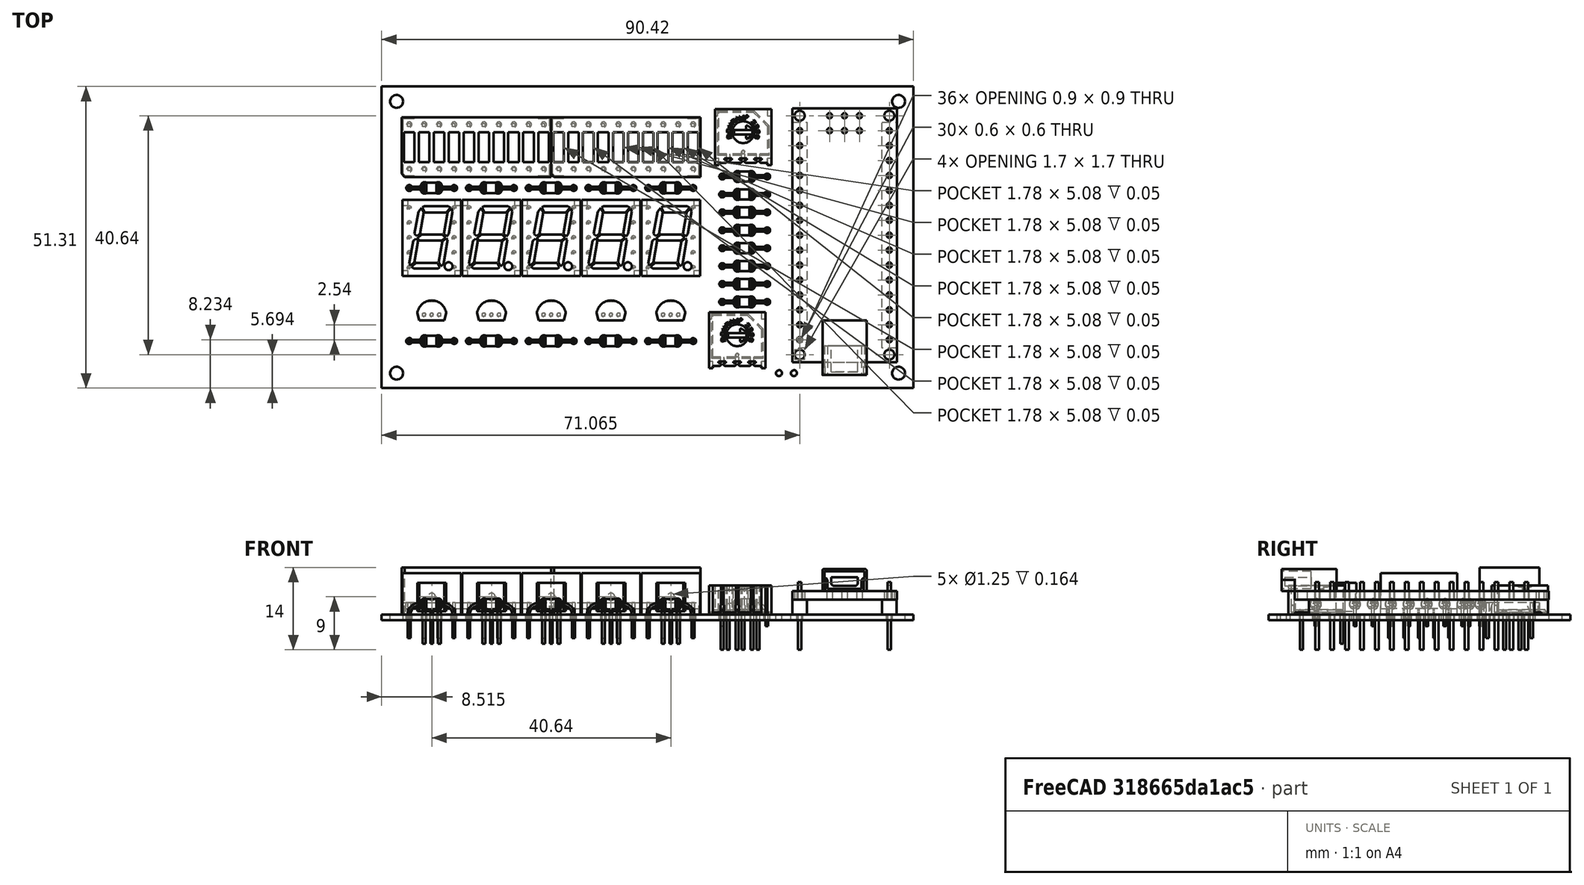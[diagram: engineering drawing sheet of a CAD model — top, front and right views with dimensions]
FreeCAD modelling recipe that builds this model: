
FCSTD DOCUMENT  (FreeCAD 0.16R6707 (Git))
Label: BobaChest
License: All rights reserved
LicenseURL: http://en.wikipedia.org/wiki/All_rights_reserved
objects: Part::Feature×202, Part::Extrusion×187, Part::FeaturePython×29, Drawing::FeatureViewPython×10, App::FeaturePython×8, Part::Compound×4, Part::Part2DObjectPython×2, Drawing::FeatureViewPart×2, Part::MultiFuse×1, Part::Cut×1, App::DocumentObjectGroup×1, Drawing::FeaturePage×1
note: 426 computed .brp shape members not serialized (recipe doc carries the construction recipe); baked Part::Feature solids carry a one-line shape summary decoded from their .brp

FEATURE [Part::Feature] Circle052
  Placement = pos=(33400,-20200,0) rot=(0,0,1;0rad)
  shape: bbox 2.429 x 2.656 x 2e-07 mm, 0 faces, 0 solids (baked)
FEATURE [Part::Feature] Circle053
  Placement = pos=(33400,-38400,0) rot=(0,0,1;0rad)
  shape: bbox 2.429 x 2.656 x 2e-07 mm, 0 faces, 0 solids (baked)
FEATURE [Part::Feature] Circle054
  Placement = pos=(67000,-20200,0) rot=(0,0,1;0rad)
  shape: bbox 2.429 x 2.656 x 2e-07 mm, 0 faces, 0 solids (baked)
FEATURE [Part::Feature] Circle055
  Placement = pos=(67000,-38400,0) rot=(0,0,1;0rad)
  shape: bbox 2.429 x 2.656 x 2e-07 mm, 0 faces, 0 solids (baked)
FEATURE [Part::Feature] Circle132
  Placement = pos=(35750,-34500,0) rot=(0,0,1;0rad)
  shape: bbox 0.701 x 0.7666 x 2e-07 mm, 0 faces, 0 solids (baked)
FEATURE [Part::Feature] Circle133
  Placement = pos=(36250,-34500,0) rot=(0,0,1;0rad)
  shape: bbox 0.701 x 0.7666 x 2e-07 mm, 0 faces, 0 solids (baked)
FEATURE [Part::Feature] Circle134
  Placement = pos=(35250,-34500,0) rot=(0,0,1;0rad)
  shape: bbox 0.701 x 0.7666 x 2e-07 mm, 0 faces, 0 solids (baked)
FEATURE [Part::Feature] Circle135
  Placement = pos=(51750,-34500,0) rot=(0,0,1;0rad)
  shape: bbox 0.701 x 0.7666 x 2e-07 mm, 0 faces, 0 solids (baked)
FEATURE [Part::Feature] Circle136
  Placement = pos=(52250,-34500,0) rot=(0,0,1;0rad)
  shape: bbox 0.701 x 0.7666 x 2e-07 mm, 0 faces, 0 solids (baked)
FEATURE [Part::Feature] Circle137
  Placement = pos=(51250,-34500,0) rot=(0,0,1;0rad)
  shape: bbox 0.701 x 0.7666 x 2e-07 mm, 0 faces, 0 solids (baked)
FEATURE [Part::Feature] Circle138
  Placement = pos=(57200,-36200,0) rot=(0,0,1;0rad)
  shape: bbox 0.701 x 0.7666 x 2e-07 mm, 0 faces, 0 solids (baked)
FEATURE [Part::Feature] Circle139
  Placement = pos=(55200,-36200,0) rot=(0,0,1;0rad)
  shape: bbox 0.701 x 0.7666 x 2e-07 mm, 0 faces, 0 solids (baked)
FEATURE [Part::Feature] Circle140
  Placement = pos=(56200,-37200,0) rot=(0,0,1;0rad)
  shape: bbox 0.701 x 0.7666 x 2e-07 mm, 0 faces, 0 solids (baked)
FEATURE [Part::Feature] Circle141
  Placement = pos=(66380,-36160,0) rot=(0,0,1;0rad)
  shape: bbox 1.122 x 1.227 x 2e-07 mm, 0 faces, 0 solids (baked)
FEATURE [Part::Feature] Circle142
  Placement = pos=(66380,-35160,0) rot=(0,0,1;0rad)
  shape: bbox 1.122 x 1.227 x 2e-07 mm, 0 faces, 0 solids (baked)
FEATURE [Part::Feature] Circle143
  Placement = pos=(66380,-34160,0) rot=(0,0,1;0rad)
  shape: bbox 1.122 x 1.227 x 2e-07 mm, 0 faces, 0 solids (baked)
FEATURE [Part::Feature] Circle144
  Placement = pos=(66380,-33160,0) rot=(0,0,1;0rad)
  shape: bbox 1.122 x 1.227 x 2e-07 mm, 0 faces, 0 solids (baked)
FEATURE [Part::Feature] Circle145
  Placement = pos=(66380,-32160,0) rot=(0,0,1;0rad)
  shape: bbox 1.122 x 1.227 x 2e-07 mm, 0 faces, 0 solids (baked)
FEATURE [Part::Feature] Circle146
  Placement = pos=(66380,-31160,0) rot=(0,0,1;0rad)
  shape: bbox 1.122 x 1.227 x 2e-07 mm, 0 faces, 0 solids (baked)
FEATURE [Part::Feature] Circle147
  Placement = pos=(66380,-30160,0) rot=(0,0,1;0rad)
  shape: bbox 1.122 x 1.227 x 2e-07 mm, 0 faces, 0 solids (baked)
FEATURE [Part::Feature] Circle148
  Placement = pos=(66380,-29160,0) rot=(0,0,1;0rad)
  shape: bbox 1.122 x 1.227 x 2e-07 mm, 0 faces, 0 solids (baked)
FEATURE [Part::Feature] Circle149
  Placement = pos=(66380,-28160,0) rot=(0,0,1;0rad)
  shape: bbox 1.122 x 1.227 x 2e-07 mm, 0 faces, 0 solids (baked)
FEATURE [Part::Feature] Circle150
  Placement = pos=(66380,-27160,0) rot=(0,0,1;0rad)
  shape: bbox 1.122 x 1.227 x 2e-07 mm, 0 faces, 0 solids (baked)
FEATURE [Part::Feature] Circle151
  Placement = pos=(66380,-26160,0) rot=(0,0,1;0rad)
  shape: bbox 1.122 x 1.227 x 2e-07 mm, 0 faces, 0 solids (baked)
FEATURE [Part::Feature] Circle152
  Placement = pos=(66380,-25160,0) rot=(0,0,1;0rad)
  shape: bbox 1.122 x 1.227 x 2e-07 mm, 0 faces, 0 solids (baked)
FEATURE [Part::Feature] Circle153
  Placement = pos=(66380,-24160,0) rot=(0,0,1;0rad)
  shape: bbox 1.122 x 1.227 x 2e-07 mm, 0 faces, 0 solids (baked)
FEATURE [Part::Feature] Circle154
  Placement = pos=(66380,-23160,0) rot=(0,0,1;0rad)
  shape: bbox 1.122 x 1.227 x 2e-07 mm, 0 faces, 0 solids (baked)
FEATURE [Part::Feature] Circle155
  Placement = pos=(66380,-22160,0) rot=(0,0,1;0rad)
  shape: bbox 1.122 x 1.227 x 2e-07 mm, 0 faces, 0 solids (baked)
FEATURE [Part::Feature] Circle156
  Placement = pos=(60380,-22160,0) rot=(0,0,1;0rad)
  shape: bbox 1.122 x 1.227 x 2e-07 mm, 0 faces, 0 solids (baked)
FEATURE [Part::Feature] Circle157
  Placement = pos=(60380,-23160,0) rot=(0,0,1;0rad)
  shape: bbox 1.122 x 1.227 x 2e-07 mm, 0 faces, 0 solids (baked)
FEATURE [Part::Feature] Circle158
  Placement = pos=(60380,-24160,0) rot=(0,0,1;0rad)
  shape: bbox 1.122 x 1.227 x 2e-07 mm, 0 faces, 0 solids (baked)
FEATURE [Part::Feature] Circle159
  Placement = pos=(60380,-25160,0) rot=(0,0,1;0rad)
  shape: bbox 1.122 x 1.227 x 2e-07 mm, 0 faces, 0 solids (baked)
FEATURE [Part::Feature] Circle160
  Placement = pos=(60380,-26160,0) rot=(0,0,1;0rad)
  shape: bbox 1.122 x 1.227 x 2e-07 mm, 0 faces, 0 solids (baked)
FEATURE [Part::Feature] Circle161
  Placement = pos=(60380,-27160,0) rot=(0,0,1;0rad)
  shape: bbox 1.122 x 1.227 x 2e-07 mm, 0 faces, 0 solids (baked)
FEATURE [Part::Feature] Circle162
  Placement = pos=(60380,-28160,0) rot=(0,0,1;0rad)
  shape: bbox 1.122 x 1.227 x 2e-07 mm, 0 faces, 0 solids (baked)
FEATURE [Part::Feature] Circle163
  Placement = pos=(60380,-29160,0) rot=(0,0,1;0rad)
  shape: bbox 1.122 x 1.227 x 2e-07 mm, 0 faces, 0 solids (baked)
FEATURE [Part::Feature] Circle164
  Placement = pos=(60380,-30160,0) rot=(0,0,1;0rad)
  shape: bbox 1.122 x 1.227 x 2e-07 mm, 0 faces, 0 solids (baked)
FEATURE [Part::Feature] Circle165
  Placement = pos=(60380,-31160,0) rot=(0,0,1;0rad)
  shape: bbox 1.122 x 1.227 x 2e-07 mm, 0 faces, 0 solids (baked)
FEATURE [Part::Feature] Circle166
  Placement = pos=(60380,-32160,0) rot=(0,0,1;0rad)
  shape: bbox 1.122 x 1.227 x 2e-07 mm, 0 faces, 0 solids (baked)
FEATURE [Part::Feature] Circle167
  Placement = pos=(60380,-33160,0) rot=(0,0,1;0rad)
  shape: bbox 1.122 x 1.227 x 2e-07 mm, 0 faces, 0 solids (baked)
FEATURE [Part::Feature] Circle168
  Placement = pos=(60380,-34160,0) rot=(0,0,1;0rad)
  shape: bbox 1.122 x 1.227 x 2e-07 mm, 0 faces, 0 solids (baked)
FEATURE [Part::Feature] Circle169
  Placement = pos=(60380,-35160,0) rot=(0,0,1;0rad)
  shape: bbox 1.122 x 1.227 x 2e-07 mm, 0 faces, 0 solids (baked)
FEATURE [Part::Feature] Circle170
  Placement = pos=(60380,-36160,0) rot=(0,0,1;0rad)
  shape: bbox 1.122 x 1.227 x 2e-07 mm, 0 faces, 0 solids (baked)
FEATURE [Part::Feature] Circle171
  Placement = pos=(39750,-34500,0) rot=(0,0,1;0rad)
  shape: bbox 0.701 x 0.7666 x 2e-07 mm, 0 faces, 0 solids (baked)
FEATURE [Part::Feature] Circle172
  Placement = pos=(40250,-34500,0) rot=(0,0,1;0rad)
  shape: bbox 0.701 x 0.7666 x 2e-07 mm, 0 faces, 0 solids (baked)
FEATURE [Part::Feature] Circle173
  Placement = pos=(39250,-34500,0) rot=(0,0,1;0rad)
  shape: bbox 0.701 x 0.7666 x 2e-07 mm, 0 faces, 0 solids (baked)
FEATURE [Part::Feature] Circle174
  Placement = pos=(43750,-34500,0) rot=(0,0,1;0rad)
  shape: bbox 0.701 x 0.7666 x 2e-07 mm, 0 faces, 0 solids (baked)
FEATURE [Part::Feature] Circle175
  Placement = pos=(44250,-34500,0) rot=(0,0,1;0rad)
  shape: bbox 0.701 x 0.7666 x 2e-07 mm, 0 faces, 0 solids (baked)
FEATURE [Part::Feature] Circle176
  Placement = pos=(43250,-34500,0) rot=(0,0,1;0rad)
  shape: bbox 0.701 x 0.7666 x 2e-07 mm, 0 faces, 0 solids (baked)
FEATURE [Part::Feature] Circle177
  Placement = pos=(47750,-34500,0) rot=(0,0,1;0rad)
  shape: bbox 0.701 x 0.7666 x 2e-07 mm, 0 faces, 0 solids (baked)
FEATURE [Part::Feature] Circle178
  Placement = pos=(48250,-34500,0) rot=(0,0,1;0rad)
  shape: bbox 0.701 x 0.7666 x 2e-07 mm, 0 faces, 0 solids (baked)
FEATURE [Part::Feature] Circle179
  Placement = pos=(47250,-34500,0) rot=(0,0,1;0rad)
  shape: bbox 0.701 x 0.7666 x 2e-07 mm, 0 faces, 0 solids (baked)
FEATURE [Part::Feature] Circle180
  Placement = pos=(42250,-27345.3,0) rot=(0,0,1;0rad)
  shape: bbox 0.8413 x 0.9199 x 2e-07 mm, 0 faces, 0 solids (baked)
FEATURE [Part::Feature] Circle181
  Placement = pos=(45250,-27345.3,0) rot=(0,0,1;0rad)
  shape: bbox 0.8413 x 0.9199 x 2e-07 mm, 0 faces, 0 solids (baked)
FEATURE [Part::Feature] Circle182
  Placement = pos=(42250,-28345.3,0) rot=(0,0,1;0rad)
  shape: bbox 0.8413 x 0.9199 x 2e-07 mm, 0 faces, 0 solids (baked)
FEATURE [Part::Feature] Circle183
  Placement = pos=(45250,-28345.3,0) rot=(0,0,1;0rad)
  shape: bbox 0.8413 x 0.9199 x 2e-07 mm, 0 faces, 0 solids (baked)
FEATURE [Part::Feature] Circle184
  Placement = pos=(42250,-29345.3,0) rot=(0,0,1;0rad)
  shape: bbox 0.8413 x 0.9199 x 2e-07 mm, 0 faces, 0 solids (baked)
FEATURE [Part::Feature] Circle185
  Placement = pos=(45250,-29345.3,0) rot=(0,0,1;0rad)
  shape: bbox 0.8413 x 0.9199 x 2e-07 mm, 0 faces, 0 solids (baked)
FEATURE [Part::Feature] Circle186
  Placement = pos=(42250,-30345.3,0) rot=(0,0,1;0rad)
  shape: bbox 0.8413 x 0.9199 x 2e-07 mm, 0 faces, 0 solids (baked)
FEATURE [Part::Feature] Circle187
  Placement = pos=(45250,-30345.3,0) rot=(0,0,1;0rad)
  shape: bbox 0.8413 x 0.9199 x 2e-07 mm, 0 faces, 0 solids (baked)
FEATURE [Part::Feature] Circle188
  Placement = pos=(42250,-31345.3,0) rot=(0,0,1;0rad)
  shape: bbox 0.8413 x 0.9199 x 2e-07 mm, 0 faces, 0 solids (baked)
FEATURE [Part::Feature] Circle189
  Placement = pos=(45250,-31345.3,0) rot=(0,0,1;0rad)
  shape: bbox 0.8413 x 0.9199 x 2e-07 mm, 0 faces, 0 solids (baked)
FEATURE [Part::Feature] Circle190
  Placement = pos=(50250,-27345.3,0) rot=(0,0,1;0rad)
  shape: bbox 0.8413 x 0.9199 x 2e-07 mm, 0 faces, 0 solids (baked)
FEATURE [Part::Feature] Circle191
  Placement = pos=(53250,-27345.3,0) rot=(0,0,1;0rad)
  shape: bbox 0.8413 x 0.9199 x 2e-07 mm, 0 faces, 0 solids (baked)
FEATURE [Part::Feature] Circle192
  Placement = pos=(50250,-28345.3,0) rot=(0,0,1;0rad)
  shape: bbox 0.8413 x 0.9199 x 2e-07 mm, 0 faces, 0 solids (baked)
FEATURE [Part::Feature] Circle193
  Placement = pos=(53250,-28345.3,0) rot=(0,0,1;0rad)
  shape: bbox 0.8413 x 0.9199 x 2e-07 mm, 0 faces, 0 solids (baked)
FEATURE [Part::Feature] Circle194
  Placement = pos=(50250,-29345.3,0) rot=(0,0,1;0rad)
  shape: bbox 0.8413 x 0.9199 x 2e-07 mm, 0 faces, 0 solids (baked)
FEATURE [Part::Feature] Circle195
  Placement = pos=(53250,-29345.3,0) rot=(0,0,1;0rad)
  shape: bbox 0.8413 x 0.9199 x 2e-07 mm, 0 faces, 0 solids (baked)
FEATURE [Part::Feature] Circle196
  Placement = pos=(50250,-30345.3,0) rot=(0,0,1;0rad)
  shape: bbox 0.8413 x 0.9199 x 2e-07 mm, 0 faces, 0 solids (baked)
FEATURE [Part::Feature] Circle197
  Placement = pos=(53250,-30345.3,0) rot=(0,0,1;0rad)
  shape: bbox 0.8413 x 0.9199 x 2e-07 mm, 0 faces, 0 solids (baked)
FEATURE [Part::Feature] Circle198
  Placement = pos=(50250,-31345.3,0) rot=(0,0,1;0rad)
  shape: bbox 0.8413 x 0.9199 x 2e-07 mm, 0 faces, 0 solids (baked)
FEATURE [Part::Feature] Circle199
  Placement = pos=(53250,-31345.3,0) rot=(0,0,1;0rad)
  shape: bbox 0.8413 x 0.9199 x 2e-07 mm, 0 faces, 0 solids (baked)
FEATURE [Part::Feature] Circle200
  Placement = pos=(46250,-27345.3,0) rot=(0,0,1;0rad)
  shape: bbox 0.8413 x 0.9199 x 2e-07 mm, 0 faces, 0 solids (baked)
FEATURE [Part::Feature] Circle201
  Placement = pos=(49250,-27345.3,0) rot=(0,0,1;0rad)
  shape: bbox 0.8413 x 0.9199 x 2e-07 mm, 0 faces, 0 solids (baked)
FEATURE [Part::Feature] Circle202
  Placement = pos=(46250,-28345.3,0) rot=(0,0,1;0rad)
  shape: bbox 0.8413 x 0.9199 x 2e-07 mm, 0 faces, 0 solids (baked)
FEATURE [Part::Feature] Circle203
  Placement = pos=(49250,-28345.3,0) rot=(0,0,1;0rad)
  shape: bbox 0.8413 x 0.9199 x 2e-07 mm, 0 faces, 0 solids (baked)
FEATURE [Part::Feature] Circle204
  Placement = pos=(46250,-29345.3,0) rot=(0,0,1;0rad)
  shape: bbox 0.8413 x 0.9199 x 2e-07 mm, 0 faces, 0 solids (baked)
FEATURE [Part::Feature] Circle205
  Placement = pos=(49250,-29345.3,0) rot=(0,0,1;0rad)
  shape: bbox 0.8413 x 0.9199 x 2e-07 mm, 0 faces, 0 solids (baked)
FEATURE [Part::Feature] Circle206
  Placement = pos=(46250,-30345.3,0) rot=(0,0,1;0rad)
  shape: bbox 0.8413 x 0.9199 x 2e-07 mm, 0 faces, 0 solids (baked)
FEATURE [Part::Feature] Circle207
  Placement = pos=(49250,-30345.3,0) rot=(0,0,1;0rad)
  shape: bbox 0.8413 x 0.9199 x 2e-07 mm, 0 faces, 0 solids (baked)
FEATURE [Part::Feature] Circle208
  Placement = pos=(46250,-31345.3,0) rot=(0,0,1;0rad)
  shape: bbox 0.8413 x 0.9199 x 2e-07 mm, 0 faces, 0 solids (baked)
FEATURE [Part::Feature] Circle209
  Placement = pos=(49250,-31345.3,0) rot=(0,0,1;0rad)
  shape: bbox 0.8413 x 0.9199 x 2e-07 mm, 0 faces, 0 solids (baked)
FEATURE [Part::Feature] Circle210
  Placement = pos=(38250,-27345.3,0) rot=(0,0,1;0rad)
  shape: bbox 0.8413 x 0.9199 x 2e-07 mm, 0 faces, 0 solids (baked)
FEATURE [Part::Feature] Circle211
  Placement = pos=(41250,-27345.3,0) rot=(0,0,1;0rad)
  shape: bbox 0.8413 x 0.9199 x 2e-07 mm, 0 faces, 0 solids (baked)
FEATURE [Part::Feature] Circle212
  Placement = pos=(38250,-28345.3,0) rot=(0,0,1;0rad)
  shape: bbox 0.8413 x 0.9199 x 2e-07 mm, 0 faces, 0 solids (baked)
FEATURE [Part::Feature] Circle213
  Placement = pos=(41250,-28345.3,0) rot=(0,0,1;0rad)
  shape: bbox 0.8413 x 0.9199 x 2e-07 mm, 0 faces, 0 solids (baked)
FEATURE [Part::Feature] Circle214
  Placement = pos=(38250,-29345.3,0) rot=(0,0,1;0rad)
  shape: bbox 0.8413 x 0.9199 x 2e-07 mm, 0 faces, 0 solids (baked)
FEATURE [Part::Feature] Circle215
  Placement = pos=(41250,-29345.3,0) rot=(0,0,1;0rad)
  shape: bbox 0.8413 x 0.9199 x 2e-07 mm, 0 faces, 0 solids (baked)
FEATURE [Part::Feature] Circle216
  Placement = pos=(38250,-30345.3,0) rot=(0,0,1;0rad)
  shape: bbox 0.8413 x 0.9199 x 2e-07 mm, 0 faces, 0 solids (baked)
FEATURE [Part::Feature] Circle217
  Placement = pos=(41250,-30345.3,0) rot=(0,0,1;0rad)
  shape: bbox 0.8413 x 0.9199 x 2e-07 mm, 0 faces, 0 solids (baked)
FEATURE [Part::Feature] Circle218
  Placement = pos=(38250,-31345.3,0) rot=(0,0,1;0rad)
  shape: bbox 0.8413 x 0.9199 x 2e-07 mm, 0 faces, 0 solids (baked)
FEATURE [Part::Feature] Circle219
  Placement = pos=(41250,-31345.3,0) rot=(0,0,1;0rad)
  shape: bbox 0.8413 x 0.9199 x 2e-07 mm, 0 faces, 0 solids (baked)
FEATURE [Part::Feature] Circle220
  Placement = pos=(34250,-27345.3,0) rot=(0,0,1;0rad)
  shape: bbox 0.8413 x 0.9199 x 2e-07 mm, 0 faces, 0 solids (baked)
FEATURE [Part::Feature] Circle221
  Placement = pos=(37250,-27345.3,0) rot=(0,0,1;0rad)
  shape: bbox 0.8413 x 0.9199 x 2e-07 mm, 0 faces, 0 solids (baked)
FEATURE [Part::Feature] Circle222
  Placement = pos=(34250,-28345.3,0) rot=(0,0,1;0rad)
  shape: bbox 0.8413 x 0.9199 x 2e-07 mm, 0 faces, 0 solids (baked)
FEATURE [Part::Feature] Circle223
  Placement = pos=(37250,-28345.3,0) rot=(0,0,1;0rad)
  shape: bbox 0.8413 x 0.9199 x 2e-07 mm, 0 faces, 0 solids (baked)
FEATURE [Part::Feature] Circle224
  Placement = pos=(34250,-29345.3,0) rot=(0,0,1;0rad)
  shape: bbox 0.8413 x 0.9199 x 2e-07 mm, 0 faces, 0 solids (baked)
FEATURE [Part::Feature] Circle225
  Placement = pos=(37250,-29345.3,0) rot=(0,0,1;0rad)
  shape: bbox 0.8413 x 0.9199 x 2e-07 mm, 0 faces, 0 solids (baked)
FEATURE [Part::Feature] Circle226
  Placement = pos=(34250,-30345.3,0) rot=(0,0,1;0rad)
  shape: bbox 0.8413 x 0.9199 x 2e-07 mm, 0 faces, 0 solids (baked)
FEATURE [Part::Feature] Circle227
  Placement = pos=(37250,-30345.3,0) rot=(0,0,1;0rad)
  shape: bbox 0.8413 x 0.9199 x 2e-07 mm, 0 faces, 0 solids (baked)
FEATURE [Part::Feature] Circle228
  Placement = pos=(34250,-31345.3,0) rot=(0,0,1;0rad)
  shape: bbox 0.8413 x 0.9199 x 2e-07 mm, 0 faces, 0 solids (baked)
FEATURE [Part::Feature] Circle229
  Placement = pos=(37250,-31345.3,0) rot=(0,0,1;0rad)
  shape: bbox 0.8413 x 0.9199 x 2e-07 mm, 0 faces, 0 solids (baked)
FEATURE [Part::Feature] Circle230
  Placement = pos=(60000,-38400,0) rot=(0,0,1;0rad)
  shape: bbox 1.122 x 1.227 x 2e-07 mm, 0 faces, 0 solids (baked)
FEATURE [Part::Feature] Circle231
  Placement = pos=(59000,-38400,0) rot=(0,0,1;0rad)
  shape: bbox 1.122 x 1.227 x 2e-07 mm, 0 faces, 0 solids (baked)
FEATURE [Part::Feature] Circle232
  Placement = pos=(33400,-20200,0) rot=(0,0,1;0rad)
  shape: bbox 2.429 x 2.656 x 2e-07 mm, 0 faces, 0 solids (baked)
FEATURE [Part::Feature] Circle233
  Placement = pos=(33400,-38400,0) rot=(0,0,1;0rad)
  shape: bbox 2.429 x 2.656 x 2e-07 mm, 0 faces, 0 solids (baked)
FEATURE [Part::Feature] Circle234
  Placement = pos=(67000,-20200,0) rot=(0,0,1;0rad)
  shape: bbox 2.429 x 2.656 x 2e-07 mm, 0 faces, 0 solids (baked)
FEATURE [Part::Feature] Circle235
  Placement = pos=(67000,-38400,0) rot=(0,0,1;0rad)
  shape: bbox 2.429 x 2.656 x 2e-07 mm, 0 faces, 0 solids (baked)
FEATURE [Part::Feature] Circle237
  Placement = pos=(35250,-24750,0) rot=(0,0,1;0rad)
  shape: bbox 1.01 x 1.104 x 2e-07 mm, 0 faces, 0 solids (baked)
FEATURE [Part::Feature] Circle238
  Placement = pos=(36250,-24750,0) rot=(0,0,1;0rad)
  shape: bbox 1.01 x 1.104 x 2e-07 mm, 0 faces, 0 solids (baked)
FEATURE [Part::Feature] Circle239
  Placement = pos=(37250,-24750,0) rot=(0,0,1;0rad)
  shape: bbox 1.01 x 1.104 x 2e-07 mm, 0 faces, 0 solids (baked)
FEATURE [Part::Feature] Circle240
  Placement = pos=(41250,-21750,0) rot=(0,0,1;0rad)
  shape: bbox 1.01 x 1.104 x 2e-07 mm, 0 faces, 0 solids (baked)
FEATURE [Part::Feature] Circle241
  Placement = pos=(40250,-21750,0) rot=(0,0,1;0rad)
  shape: bbox 1.01 x 1.104 x 2e-07 mm, 0 faces, 0 solids (baked)
FEATURE [Part::Feature] Circle242
  Placement = pos=(39250,-21750,0) rot=(0,0,1;0rad)
  shape: bbox 1.01 x 1.104 x 2e-07 mm, 0 faces, 0 solids (baked)
FEATURE [Part::Feature] Circle243
  Placement = pos=(38250,-21750,0) rot=(0,0,1;0rad)
  shape: bbox 1.01 x 1.104 x 2e-07 mm, 0 faces, 0 solids (baked)
FEATURE [Part::Feature] Circle244
  Placement = pos=(38250,-24750,0) rot=(0,0,1;0rad)
  shape: bbox 1.01 x 1.104 x 2e-07 mm, 0 faces, 0 solids (baked)
FEATURE [Part::Feature] Circle245
  Placement = pos=(39250,-24750,0) rot=(0,0,1;0rad)
  shape: bbox 1.01 x 1.104 x 2e-07 mm, 0 faces, 0 solids (baked)
FEATURE [Part::Feature] Circle246
  Placement = pos=(40250,-24750,0) rot=(0,0,1;0rad)
  shape: bbox 1.01 x 1.104 x 2e-07 mm, 0 faces, 0 solids (baked)
FEATURE [Part::Feature] Circle247
  Placement = pos=(41250,-24750,0) rot=(0,0,1;0rad)
  shape: bbox 1.01 x 1.104 x 2e-07 mm, 0 faces, 0 solids (baked)
FEATURE [Part::Feature] Circle248
  Placement = pos=(42250,-21750,0) rot=(0,0,1;0rad)
  shape: bbox 1.01 x 1.104 x 2e-07 mm, 0 faces, 0 solids (baked)
FEATURE [Part::Feature] Circle249
  Placement = pos=(43250,-21750,0) rot=(0,0,1;0rad)
  shape: bbox 1.01 x 1.104 x 2e-07 mm, 0 faces, 0 solids (baked)
FEATURE [Part::Feature] Circle250
  Placement = pos=(43250,-24750,0) rot=(0,0,1;0rad)
  shape: bbox 1.01 x 1.104 x 2e-07 mm, 0 faces, 0 solids (baked)
FEATURE [Part::Feature] Circle251
  Placement = pos=(42250,-24750,0) rot=(0,0,1;0rad)
  shape: bbox 1.01 x 1.104 x 2e-07 mm, 0 faces, 0 solids (baked)
FEATURE [Part::Feature] Circle252
  Placement = pos=(37250,-21750,0) rot=(0,0,1;0rad)
  shape: bbox 1.01 x 1.104 x 2e-07 mm, 0 faces, 0 solids (baked)
FEATURE [Part::Feature] Circle253
  Placement = pos=(36250,-21750,0) rot=(0,0,1;0rad)
  shape: bbox 1.01 x 1.104 x 2e-07 mm, 0 faces, 0 solids (baked)
FEATURE [Part::Feature] Circle254
  Placement = pos=(35250,-21750,0) rot=(0,0,1;0rad)
  shape: bbox 1.01 x 1.104 x 2e-07 mm, 0 faces, 0 solids (baked)
FEATURE [Part::Feature] Circle255
  Placement = pos=(34250,-21750,0) rot=(0,0,1;0rad)
  shape: bbox 1.01 x 1.104 x 2e-07 mm, 0 faces, 0 solids (baked)
FEATURE [Part::Feature] Circle256
  Placement = pos=(44250,-24750,0) rot=(0,0,1;0rad)
  shape: bbox 1.01 x 1.104 x 2e-07 mm, 0 faces, 0 solids (baked)
FEATURE [Part::Feature] Circle257
  Placement = pos=(45250,-24750,0) rot=(0,0,1;0rad)
  shape: bbox 1.01 x 1.104 x 2e-07 mm, 0 faces, 0 solids (baked)
FEATURE [Part::Feature] Circle258
  Placement = pos=(46250,-24750,0) rot=(0,0,1;0rad)
  shape: bbox 1.01 x 1.104 x 2e-07 mm, 0 faces, 0 solids (baked)
FEATURE [Part::Feature] Circle259
  Placement = pos=(47250,-24750,0) rot=(0,0,1;0rad)
  shape: bbox 1.01 x 1.104 x 2e-07 mm, 0 faces, 0 solids (baked)
FEATURE [Part::Feature] Circle260
  Placement = pos=(51250,-21750,0) rot=(0,0,1;0rad)
  shape: bbox 1.01 x 1.104 x 2e-07 mm, 0 faces, 0 solids (baked)
FEATURE [Part::Feature] Circle261
  Placement = pos=(50250,-21750,0) rot=(0,0,1;0rad)
  shape: bbox 1.01 x 1.104 x 2e-07 mm, 0 faces, 0 solids (baked)
FEATURE [Part::Feature] Circle262
  Placement = pos=(49250,-21750,0) rot=(0,0,1;0rad)
  shape: bbox 1.01 x 1.104 x 2e-07 mm, 0 faces, 0 solids (baked)
FEATURE [Part::Feature] Circle263
  Placement = pos=(48250,-21750,0) rot=(0,0,1;0rad)
  shape: bbox 1.01 x 1.104 x 2e-07 mm, 0 faces, 0 solids (baked)
FEATURE [Part::Feature] Circle264
  Placement = pos=(48250,-24750,0) rot=(0,0,1;0rad)
  shape: bbox 1.01 x 1.104 x 2e-07 mm, 0 faces, 0 solids (baked)
FEATURE [Part::Feature] Circle265
  Placement = pos=(49250,-24750,0) rot=(0,0,1;0rad)
  shape: bbox 1.01 x 1.104 x 2e-07 mm, 0 faces, 0 solids (baked)
FEATURE [Part::Feature] Circle266
  Placement = pos=(50250,-24750,0) rot=(0,0,1;0rad)
  shape: bbox 1.01 x 1.104 x 2e-07 mm, 0 faces, 0 solids (baked)
FEATURE [Part::Feature] Circle267
  Placement = pos=(51250,-24750,0) rot=(0,0,1;0rad)
  shape: bbox 1.01 x 1.104 x 2e-07 mm, 0 faces, 0 solids (baked)
FEATURE [Part::Feature] Circle268
  Placement = pos=(52250,-21750,0) rot=(0,0,1;0rad)
  shape: bbox 1.01 x 1.104 x 2e-07 mm, 0 faces, 0 solids (baked)
FEATURE [Part::Feature] Circle269
  Placement = pos=(53250,-21750,0) rot=(0,0,1;0rad)
  shape: bbox 1.01 x 1.104 x 2e-07 mm, 0 faces, 0 solids (baked)
FEATURE [Part::Feature] Circle270
  Placement = pos=(53250,-24750,0) rot=(0,0,1;0rad)
  shape: bbox 1.01 x 1.104 x 2e-07 mm, 0 faces, 0 solids (baked)
FEATURE [Part::Feature] Circle271
  Placement = pos=(52250,-24750,0) rot=(0,0,1;0rad)
  shape: bbox 1.01 x 1.104 x 2e-07 mm, 0 faces, 0 solids (baked)
FEATURE [Part::Feature] Circle272
  Placement = pos=(47250,-21750,0) rot=(0,0,1;0rad)
  shape: bbox 1.01 x 1.104 x 2e-07 mm, 0 faces, 0 solids (baked)
FEATURE [Part::Feature] Circle273
  Placement = pos=(46250,-21750,0) rot=(0,0,1;0rad)
  shape: bbox 1.01 x 1.104 x 2e-07 mm, 0 faces, 0 solids (baked)
FEATURE [Part::Feature] Circle274
  Placement = pos=(45250,-21750,0) rot=(0,0,1;0rad)
  shape: bbox 1.01 x 1.104 x 2e-07 mm, 0 faces, 0 solids (baked)
FEATURE [Part::Feature] Circle275
  Placement = pos=(44250,-21750,0) rot=(0,0,1;0rad)
  shape: bbox 1.01 x 1.104 x 2e-07 mm, 0 faces, 0 solids (baked)
FEATURE [Part::Feature] Circle276
  Placement = pos=(57600,-22600,0) rot=(0,0,1;0rad)
  shape: bbox 0.701 x 0.7666 x 2e-07 mm, 0 faces, 0 solids (baked)
FEATURE [Part::Feature] Circle277
  Placement = pos=(55600,-22600,0) rot=(0,0,1;0rad)
  shape: bbox 0.701 x 0.7666 x 2e-07 mm, 0 faces, 0 solids (baked)
FEATURE [Part::Feature] Circle278
  Placement = pos=(56600,-23600,0) rot=(0,0,1;0rad)
  shape: bbox 0.701 x 0.7666 x 2e-07 mm, 0 faces, 0 solids (baked)
FEATURE [Part::Feature] Circle279
  Placement = pos=(55200,-26430,0) rot=(0,0,1;0rad)
  shape: bbox 1.122 x 1.227 x 2e-07 mm, 0 faces, 0 solids (baked)
FEATURE [Part::Feature] Circle280
  Placement = pos=(58200,-26430,0) rot=(0,0,1;0rad)
  shape: bbox 1.122 x 1.227 x 2e-07 mm, 0 faces, 0 solids (baked)
FEATURE [Part::Feature] Circle281
  Placement = pos=(55200,-28830,0) rot=(0,0,1;0rad)
  shape: bbox 1.122 x 1.227 x 2e-07 mm, 0 faces, 0 solids (baked)
FEATURE [Part::Feature] Circle282
  Placement = pos=(58200,-28830,0) rot=(0,0,1;0rad)
  shape: bbox 1.122 x 1.227 x 2e-07 mm, 0 faces, 0 solids (baked)
FEATURE [Part::Feature] Circle283
  Placement = pos=(55200,-31230,0) rot=(0,0,1;0rad)
  shape: bbox 1.122 x 1.227 x 2e-07 mm, 0 faces, 0 solids (baked)
FEATURE [Part::Feature] Circle284
  Placement = pos=(58200,-31230,0) rot=(0,0,1;0rad)
  shape: bbox 1.122 x 1.227 x 2e-07 mm, 0 faces, 0 solids (baked)
FEATURE [Part::Feature] Circle285
  Placement = pos=(55200,-32430,0) rot=(0,0,1;0rad)
  shape: bbox 1.122 x 1.227 x 2e-07 mm, 0 faces, 0 solids (baked)
FEATURE [Part::Feature] Circle286
  Placement = pos=(58200,-32430,0) rot=(0,0,1;0rad)
  shape: bbox 1.122 x 1.227 x 2e-07 mm, 0 faces, 0 solids (baked)
FEATURE [Part::Feature] Circle287
  Placement = pos=(55200,-30030,0) rot=(0,0,1;0rad)
  shape: bbox 1.122 x 1.227 x 2e-07 mm, 0 faces, 0 solids (baked)
FEATURE [Part::Feature] Circle288
  Placement = pos=(58200,-30030,0) rot=(0,0,1;0rad)
  shape: bbox 1.122 x 1.227 x 2e-07 mm, 0 faces, 0 solids (baked)
FEATURE [Part::Feature] Circle289
  Placement = pos=(55200,-27630,0) rot=(0,0,1;0rad)
  shape: bbox 1.122 x 1.227 x 2e-07 mm, 0 faces, 0 solids (baked)
FEATURE [Part::Feature] Circle290
  Placement = pos=(58200,-27630,0) rot=(0,0,1;0rad)
  shape: bbox 1.122 x 1.227 x 2e-07 mm, 0 faces, 0 solids (baked)
FEATURE [Part::Feature] Circle291
  Placement = pos=(55200,-25230,0) rot=(0,0,1;0rad)
  shape: bbox 1.122 x 1.227 x 2e-07 mm, 0 faces, 0 solids (baked)
FEATURE [Part::Feature] Circle292
  Placement = pos=(58200,-25230,0) rot=(0,0,1;0rad)
  shape: bbox 1.122 x 1.227 x 2e-07 mm, 0 faces, 0 solids (baked)
FEATURE [Part::Feature] Circle293
  Placement = pos=(55200,-33630,0) rot=(0,0,1;0rad)
  shape: bbox 1.122 x 1.227 x 2e-07 mm, 0 faces, 0 solids (baked)
FEATURE [Part::Feature] Circle294
  Placement = pos=(58200,-33630,0) rot=(0,0,1;0rad)
  shape: bbox 1.122 x 1.227 x 2e-07 mm, 0 faces, 0 solids (baked)
FEATURE [Part::Feature] Circle295
  Placement = pos=(50250,-26000,0) rot=(0,0,1;0rad)
  shape: bbox 1.122 x 1.227 x 2e-07 mm, 0 faces, 0 solids (baked)
FEATURE [Part::Feature] Circle296
  Placement = pos=(53250,-26000,0) rot=(0,0,1;0rad)
  shape: bbox 1.122 x 1.227 x 2e-07 mm, 0 faces, 0 solids (baked)
FEATURE [Part::Feature] Circle297
  Placement = pos=(46250,-26000,0) rot=(0,0,1;0rad)
  shape: bbox 1.122 x 1.227 x 2e-07 mm, 0 faces, 0 solids (baked)
FEATURE [Part::Feature] Circle298
  Placement = pos=(49250,-26000,0) rot=(0,0,1;0rad)
  shape: bbox 1.122 x 1.227 x 2e-07 mm, 0 faces, 0 solids (baked)
FEATURE [Part::Feature] Circle299
  Placement = pos=(42250,-26000,0) rot=(0,0,1;0rad)
  shape: bbox 1.122 x 1.227 x 2e-07 mm, 0 faces, 0 solids (baked)
FEATURE [Part::Feature] Circle300
  Placement = pos=(45250,-26000,0) rot=(0,0,1;0rad)
  shape: bbox 1.122 x 1.227 x 2e-07 mm, 0 faces, 0 solids (baked)
FEATURE [Part::Feature] Circle301
  Placement = pos=(38250,-26000,0) rot=(0,0,1;0rad)
  shape: bbox 1.122 x 1.227 x 2e-07 mm, 0 faces, 0 solids (baked)
FEATURE [Part::Feature] Circle302
  Placement = pos=(41250,-26000,0) rot=(0,0,1;0rad)
  shape: bbox 1.122 x 1.227 x 2e-07 mm, 0 faces, 0 solids (baked)
FEATURE [Part::Feature] Circle303
  Placement = pos=(34250,-26000,0) rot=(0,0,1;0rad)
  shape: bbox 1.122 x 1.227 x 2e-07 mm, 0 faces, 0 solids (baked)
FEATURE [Part::Feature] Circle304
  Placement = pos=(37250,-26000,0) rot=(0,0,1;0rad)
  shape: bbox 1.122 x 1.227 x 2e-07 mm, 0 faces, 0 solids (baked)
FEATURE [Part::Feature] Circle305
  Placement = pos=(50250,-36250,0) rot=(0,0,1;0rad)
  shape: bbox 1.122 x 1.227 x 2e-07 mm, 0 faces, 0 solids (baked)
FEATURE [Part::Feature] Circle306
  Placement = pos=(53250,-36250,0) rot=(0,0,1;0rad)
  shape: bbox 1.122 x 1.227 x 2e-07 mm, 0 faces, 0 solids (baked)
FEATURE [Part::Feature] Circle307
  Placement = pos=(46250,-36250,0) rot=(0,0,1;0rad)
  shape: bbox 1.122 x 1.227 x 2e-07 mm, 0 faces, 0 solids (baked)
FEATURE [Part::Feature] Circle308
  Placement = pos=(49250,-36250,0) rot=(0,0,1;0rad)
  shape: bbox 1.122 x 1.227 x 2e-07 mm, 0 faces, 0 solids (baked)
FEATURE [Part::Feature] Circle309
  Placement = pos=(42250,-36250,0) rot=(0,0,1;0rad)
  shape: bbox 1.122 x 1.227 x 2e-07 mm, 0 faces, 0 solids (baked)
FEATURE [Part::Feature] Circle310
  Placement = pos=(45250,-36250,0) rot=(0,0,1;0rad)
  shape: bbox 1.122 x 1.227 x 2e-07 mm, 0 faces, 0 solids (baked)
FEATURE [Part::Feature] Circle311
  Placement = pos=(38250,-36250,0) rot=(0,0,1;0rad)
  shape: bbox 1.122 x 1.227 x 2e-07 mm, 0 faces, 0 solids (baked)
FEATURE [Part::Feature] Circle312
  Placement = pos=(41250,-36250,0) rot=(0,0,1;0rad)
  shape: bbox 1.122 x 1.227 x 2e-07 mm, 0 faces, 0 solids (baked)
FEATURE [Part::Feature] Circle313
  Placement = pos=(34250,-36250,0) rot=(0,0,1;0rad)
  shape: bbox 1.122 x 1.227 x 2e-07 mm, 0 faces, 0 solids (baked)
FEATURE [Part::Feature] Circle314
  Placement = pos=(37250,-36250,0) rot=(0,0,1;0rad)
  shape: bbox 1.122 x 1.227 x 2e-07 mm, 0 faces, 0 solids (baked)
FEATURE [Part::Feature] Part__Feature  label="nano3"
  shape: bbox 43.18 x 1.5 x 17.78 mm, 86 faces (baked)
FEATURE [Part::Feature] Part__Feature001  label="hdr_m15p"
  Placement = pos=(2.39,0,-2.52) rot=(1,0,0;3.14159rad)
  shape: bbox 38.4 x 11.5 x 2.5 mm, 162 faces (baked)
FEATURE [Part::Feature] Part__Feature002  label="hdr_m15p001"
  Placement = pos=(2.39,0,-17.76) rot=(1,0,0;3.14159rad)
  shape: bbox 38.4 x 11.5 x 2.5 mm, 162 faces (baked)
FEATURE [Part::Feature] Part__Feature004  label="usb_minib"
  Placement = pos=(0,1.5,-8.89) rot=(0,-1,0;1.5708rad)
  shape: bbox 9.3 x 3.7 x 7.5 mm, 44 faces (baked)
FEATURE [Part::Feature] Part__Feature005  label="3386F"
  shape: bbox 9.576 x 9.576 x 4.953 mm, 585 faces (baked)
FEATURE [Part::Feature] Part__Feature006  label="3386F001"
  Placement = pos=(2.5,0,0) rot=(0,0,1;0rad)
  shape: bbox 0.508 x 0.508 x 6.655 mm, 4 faces (baked)
FEATURE [Part::Feature] Part__Feature007  label="3386F002"
  Placement = pos=(2.5,0,0) rot=(0,0,1;0rad)
  shape: bbox 0.508 x 0.508 x 6.655 mm, 4 faces (baked)
FEATURE [Part::Feature] Part__Feature008  label="3386F003"
  shape: bbox 0.508 x 0.508 x 6.655 mm, 4 faces (baked)
FEATURE [Part::Compound] Compound002
  Links = -> [Part__Feature005,Part__Feature006,Part__Feature007,Part__Feature008]
  Placement = pos=(142.75,-91.0843,5.953) rot=(-0.707107,0.707107,0;3.14159rad)
FEATURE [Part::Feature] Part__Feature009  label="DC-10"
  Placement = pos=(123.774,-59.1149,9) rot=(1,0,0;1.5708rad)
  shape: bbox 25.4 x 10.16 x 12 mm, 461 faces (baked)
FEATURE [Part::Compound] Compound003
  Links = -> [Part__Feature,Part__Feature001,Part__Feature002,Part__Feature004]
  Placement = pos=(169.875,-95.6563,3.5) rot=(0.57735,0.57735,0.57735;2.0944rad)
FEATURE [Part::FeaturePython] Clone  label="Clone of DC-10"  # Draft clone (typed FeaturePython)
  Objects = -> [Part__Feature009]
  Placement = pos=(98.3741,-59.1149,9) rot=(1,0,0;1.5708rad)
  Scale = (1,1,1)
FEATURE [Part::FeaturePython] Clone001  label="Clone of Compound002"  # Draft clone (typed FeaturePython)
  Objects = -> [Compound002]
  Placement = pos=(143.766,-56.5403,5.953) rot=(-0.707107,0.707107,0;3.14159rad)
  Scale = (1,1,1)
FEATURE [Part::Extrusion] Extrude
  Base = -> Circle052
  Dir = (0,0,1)
  Solid = true
FEATURE [Part::Extrusion] Extrude001
  Base = -> Circle053
  Dir = (0,0,1)
  Solid = true
FEATURE [Part::Extrusion] Extrude002
  Base = -> Circle054
  Dir = (0,0,1)
  Solid = true
FEATURE [Part::Extrusion] Extrude003
  Base = -> Circle055
  Dir = (0,0,1)
  Solid = true
FEATURE [Part::Extrusion] Extrude004
  Base = -> Circle132
  Dir = (0,0,1)
  Solid = true
FEATURE [Part::Extrusion] Extrude005
  Base = -> Circle133
  Dir = (0,0,1)
  Solid = true
FEATURE [Part::Extrusion] Extrude006
  Base = -> Circle134
  Dir = (0,0,1)
  Solid = true
FEATURE [Part::Extrusion] Extrude007
  Base = -> Circle135
  Dir = (0,0,1)
  Solid = true
FEATURE [Part::Extrusion] Extrude008
  Base = -> Circle136
  Dir = (0,0,1)
  Solid = true
FEATURE [Part::Extrusion] Extrude009
  Base = -> Circle137
  Dir = (0,0,1)
  Solid = true
FEATURE [Part::Extrusion] Extrude010
  Base = -> Circle138
  Dir = (0,0,1)
  Solid = true
FEATURE [Part::Extrusion] Extrude011
  Base = -> Circle139
  Dir = (0,0,1)
  Solid = true
FEATURE [Part::Extrusion] Extrude012
  Base = -> Circle140
  Dir = (0,0,1)
  Solid = true
FEATURE [Part::Extrusion] Extrude013
  Base = -> Circle141
  Dir = (0,0,1)
  Solid = true
FEATURE [Part::Extrusion] Extrude014
  Base = -> Circle142
  Dir = (0,0,1)
  Solid = true
FEATURE [Part::Extrusion] Extrude015
  Base = -> Circle143
  Dir = (0,0,1)
  Solid = true
FEATURE [Part::Extrusion] Extrude016
  Base = -> Circle144
  Dir = (0,0,1)
  Solid = true
FEATURE [Part::Extrusion] Extrude017
  Base = -> Circle145
  Dir = (0,0,1)
  Solid = true
FEATURE [Part::Extrusion] Extrude018
  Base = -> Circle146
  Dir = (0,0,1)
  Solid = true
FEATURE [Part::Extrusion] Extrude019
  Base = -> Circle147
  Dir = (0,0,1)
  Solid = true
FEATURE [Part::Extrusion] Extrude020
  Base = -> Circle148
  Dir = (0,0,1)
  Solid = true
FEATURE [Part::Extrusion] Extrude021
  Base = -> Circle149
  Dir = (0,0,1)
  Solid = true
FEATURE [Part::Extrusion] Extrude022
  Base = -> Circle150
  Dir = (0,0,1)
  Solid = true
FEATURE [Part::Extrusion] Extrude023
  Base = -> Circle151
  Dir = (0,0,1)
  Solid = true
FEATURE [Part::Extrusion] Extrude024
  Base = -> Circle152
  Dir = (0,0,1)
  Solid = true
FEATURE [Part::Extrusion] Extrude025
  Base = -> Circle153
  Dir = (0,0,1)
  Solid = true
FEATURE [Part::Extrusion] Extrude026
  Base = -> Circle154
  Dir = (0,0,1)
  Solid = true
FEATURE [Part::Extrusion] Extrude027
  Base = -> Circle155
  Dir = (0,0,1)
  Solid = true
FEATURE [Part::Extrusion] Extrude028
  Base = -> Circle156
  Dir = (0,0,1)
  Solid = true
FEATURE [Part::Extrusion] Extrude029
  Base = -> Circle157
  Dir = (0,0,1)
  Solid = true
FEATURE [Part::Extrusion] Extrude030
  Base = -> Circle158
  Dir = (0,0,1)
  Solid = true
FEATURE [Part::Extrusion] Extrude031
  Base = -> Circle159
  Dir = (0,0,1)
  Solid = true
FEATURE [Part::Extrusion] Extrude032
  Base = -> Circle160
  Dir = (0,0,1)
  Solid = true
FEATURE [Part::Extrusion] Extrude033
  Base = -> Circle161
  Dir = (0,0,1)
  Solid = true
FEATURE [Part::Extrusion] Extrude034
  Base = -> Circle162
  Dir = (0,0,1)
  Solid = true
FEATURE [Part::Extrusion] Extrude035
  Base = -> Circle163
  Dir = (0,0,1)
  Solid = true
FEATURE [Part::Extrusion] Extrude036
  Base = -> Circle164
  Dir = (0,0,1)
  Solid = true
FEATURE [Part::Extrusion] Extrude037
  Base = -> Circle165
  Dir = (0,0,1)
  Solid = true
FEATURE [Part::Extrusion] Extrude038
  Base = -> Circle166
  Dir = (0,0,1)
  Solid = true
FEATURE [Part::Extrusion] Extrude039
  Base = -> Circle167
  Dir = (0,0,1)
  Solid = true
FEATURE [Part::Extrusion] Extrude040
  Base = -> Circle168
  Dir = (0,0,1)
  Solid = true
FEATURE [Part::Extrusion] Extrude041
  Base = -> Circle169
  Dir = (0,0,1)
  Solid = true
FEATURE [Part::Extrusion] Extrude042
  Base = -> Circle170
  Dir = (0,0,1)
  Solid = true
FEATURE [Part::Extrusion] Extrude043
  Base = -> Circle171
  Dir = (0,0,1)
  Solid = true
FEATURE [Part::Extrusion] Extrude044
  Base = -> Circle172
  Dir = (0,0,1)
  Solid = true
FEATURE [Part::Extrusion] Extrude045
  Base = -> Circle173
  Dir = (0,0,1)
  Solid = true
FEATURE [Part::Extrusion] Extrude046
  Base = -> Circle174
  Dir = (0,0,1)
  Solid = true
FEATURE [Part::Extrusion] Extrude047
  Base = -> Circle175
  Dir = (0,0,1)
  Solid = true
FEATURE [Part::Extrusion] Extrude048
  Base = -> Circle176
  Dir = (0,0,1)
  Solid = true
FEATURE [Part::Extrusion] Extrude049
  Base = -> Circle177
  Dir = (0,0,1)
  Solid = true
FEATURE [Part::Extrusion] Extrude050
  Base = -> Circle178
  Dir = (0,0,1)
  Solid = true
FEATURE [Part::Extrusion] Extrude051
  Base = -> Circle179
  Dir = (0,0,1)
  Solid = true
FEATURE [Part::Extrusion] Extrude052
  Base = -> Circle180
  Dir = (0,0,1)
  Solid = true
FEATURE [Part::Extrusion] Extrude053
  Base = -> Circle181
  Dir = (0,0,1)
  Solid = true
FEATURE [Part::Extrusion] Extrude054
  Base = -> Circle182
  Dir = (0,0,1)
  Solid = true
FEATURE [Part::Extrusion] Extrude055
  Base = -> Circle183
  Dir = (0,0,1)
  Solid = true
FEATURE [Part::Extrusion] Extrude056
  Base = -> Circle184
  Dir = (0,0,1)
  Solid = true
FEATURE [Part::Extrusion] Extrude057
  Base = -> Circle185
  Dir = (0,0,1)
  Solid = true
FEATURE [Part::Extrusion] Extrude058
  Base = -> Circle186
  Dir = (0,0,1)
  Solid = true
FEATURE [Part::Extrusion] Extrude059
  Base = -> Circle187
  Dir = (0,0,1)
  Solid = true
FEATURE [Part::Extrusion] Extrude060
  Base = -> Circle188
  Dir = (0,0,1)
  Solid = true
FEATURE [Part::Extrusion] Extrude061
  Base = -> Circle189
  Dir = (0,0,1)
  Solid = true
FEATURE [Part::Extrusion] Extrude062
  Base = -> Circle190
  Dir = (0,0,1)
  Solid = true
FEATURE [Part::Extrusion] Extrude063
  Base = -> Circle191
  Dir = (0,0,1)
  Solid = true
FEATURE [Part::Extrusion] Extrude064
  Base = -> Circle192
  Dir = (0,0,1)
  Solid = true
FEATURE [Part::Extrusion] Extrude065
  Base = -> Circle193
  Dir = (0,0,1)
  Solid = true
FEATURE [Part::Extrusion] Extrude066
  Base = -> Circle194
  Dir = (0,0,1)
  Solid = true
FEATURE [Part::Extrusion] Extrude067
  Base = -> Circle195
  Dir = (0,0,1)
  Solid = true
FEATURE [Part::Extrusion] Extrude068
  Base = -> Circle196
  Dir = (0,0,1)
  Solid = true
FEATURE [Part::Extrusion] Extrude069
  Base = -> Circle197
  Dir = (0,0,1)
  Solid = true
FEATURE [Part::Extrusion] Extrude070
  Base = -> Circle198
  Dir = (0,0,1)
  Solid = true
FEATURE [Part::Extrusion] Extrude071
  Base = -> Circle199
  Dir = (0,0,1)
  Solid = true
FEATURE [Part::Extrusion] Extrude072
  Base = -> Circle200
  Dir = (0,0,1)
  Solid = true
FEATURE [Part::Extrusion] Extrude073
  Base = -> Circle201
  Dir = (0,0,1)
  Solid = true
FEATURE [Part::Extrusion] Extrude074
  Base = -> Circle202
  Dir = (0,0,1)
  Solid = true
FEATURE [Part::Extrusion] Extrude075
  Base = -> Circle203
  Dir = (0,0,1)
  Solid = true
FEATURE [Part::Extrusion] Extrude076
  Base = -> Circle204
  Dir = (0,0,1)
  Solid = true
FEATURE [Part::Extrusion] Extrude077
  Base = -> Circle205
  Dir = (0,0,1)
  Solid = true
FEATURE [Part::Extrusion] Extrude078
  Base = -> Circle206
  Dir = (0,0,1)
  Solid = true
FEATURE [Part::Extrusion] Extrude079
  Base = -> Circle207
  Dir = (0,0,1)
  Solid = true
FEATURE [Part::Extrusion] Extrude080
  Base = -> Circle208
  Dir = (0,0,1)
  Solid = true
FEATURE [Part::Extrusion] Extrude081
  Base = -> Circle209
  Dir = (0,0,1)
  Solid = true
FEATURE [Part::Extrusion] Extrude082
  Base = -> Circle210
  Dir = (0,0,1)
  Solid = true
FEATURE [Part::Extrusion] Extrude083
  Base = -> Circle211
  Dir = (0,0,1)
  Solid = true
FEATURE [Part::Extrusion] Extrude084
  Base = -> Circle212
  Dir = (0,0,1)
  Solid = true
FEATURE [Part::Extrusion] Extrude085
  Base = -> Circle213
  Dir = (0,0,1)
  Solid = true
FEATURE [Part::Extrusion] Extrude086
  Base = -> Circle214
  Dir = (0,0,1)
  Solid = true
FEATURE [Part::Extrusion] Extrude087
  Base = -> Circle215
  Dir = (0,0,1)
  Solid = true
FEATURE [Part::Extrusion] Extrude088
  Base = -> Circle216
  Dir = (0,0,1)
  Solid = true
FEATURE [Part::Extrusion] Extrude089
  Base = -> Circle217
  Dir = (0,0,1)
  Solid = true
FEATURE [Part::Extrusion] Extrude090
  Base = -> Circle218
  Dir = (0,0,1)
  Solid = true
FEATURE [Part::Extrusion] Extrude091
  Base = -> Circle219
  Dir = (0,0,1)
  Solid = true
FEATURE [Part::Extrusion] Extrude092
  Base = -> Circle220
  Dir = (0,0,1)
  Solid = true
FEATURE [Part::Extrusion] Extrude093
  Base = -> Circle221
  Dir = (0,0,1)
  Solid = true
FEATURE [Part::Extrusion] Extrude094
  Base = -> Circle222
  Dir = (0,0,1)
  Solid = true
FEATURE [Part::Extrusion] Extrude095
  Base = -> Circle223
  Dir = (0,0,1)
  Solid = true
FEATURE [Part::Extrusion] Extrude096
  Base = -> Circle224
  Dir = (0,0,1)
  Solid = true
FEATURE [Part::Extrusion] Extrude097
  Base = -> Circle225
  Dir = (0,0,1)
  Solid = true
FEATURE [Part::Extrusion] Extrude098
  Base = -> Circle226
  Dir = (0,0,1)
  Solid = true
FEATURE [Part::Extrusion] Extrude099
  Base = -> Circle227
  Dir = (0,0,1)
  Solid = true
FEATURE [Part::Extrusion] Extrude100
  Base = -> Circle228
  Dir = (0,0,1)
  Solid = true
FEATURE [Part::Extrusion] Extrude101
  Base = -> Circle229
  Dir = (0,0,1)
  Solid = true
FEATURE [Part::Extrusion] Extrude102
  Base = -> Circle230
  Dir = (0,0,1)
  Solid = true
FEATURE [Part::Extrusion] Extrude103
  Base = -> Circle231
  Dir = (0,0,1)
  Solid = true
FEATURE [Part::Extrusion] Extrude104
  Base = -> Circle232
  Dir = (0,0,1)
  Solid = true
FEATURE [Part::Extrusion] Extrude105
  Base = -> Circle233
  Dir = (0,0,1)
  Solid = true
FEATURE [Part::Extrusion] Extrude106
  Base = -> Circle234
  Dir = (0,0,1)
  Solid = true
FEATURE [Part::Extrusion] Extrude107
  Base = -> Circle235
  Dir = (0,0,1)
  Solid = true
FEATURE [Part::Extrusion] Extrude108
  Base = -> Circle237
  Dir = (0,0,1)
  Solid = true
FEATURE [Part::Extrusion] Extrude109
  Base = -> Circle238
  Dir = (0,0,1)
  Solid = true
FEATURE [Part::Extrusion] Extrude110
  Base = -> Circle239
  Dir = (0,0,1)
  Solid = true
FEATURE [Part::Extrusion] Extrude111
  Base = -> Circle240
  Dir = (0,0,1)
  Solid = true
FEATURE [Part::Extrusion] Extrude112
  Base = -> Circle241
  Dir = (0,0,1)
  Solid = true
FEATURE [Part::Extrusion] Extrude113
  Base = -> Circle242
  Dir = (0,0,1)
  Solid = true
FEATURE [Part::Extrusion] Extrude114
  Base = -> Circle243
  Dir = (0,0,1)
  Solid = true
FEATURE [Part::Extrusion] Extrude115
  Base = -> Circle244
  Dir = (0,0,1)
  Solid = true
FEATURE [Part::Extrusion] Extrude116
  Base = -> Circle245
  Dir = (0,0,1)
  Solid = true
FEATURE [Part::Extrusion] Extrude117
  Base = -> Circle246
  Dir = (0,0,1)
  Solid = true
FEATURE [Part::Extrusion] Extrude118
  Base = -> Circle247
  Dir = (0,0,1)
  Solid = true
FEATURE [Part::Extrusion] Extrude119
  Base = -> Circle248
  Dir = (0,0,1)
  Solid = true
FEATURE [Part::Extrusion] Extrude120
  Base = -> Circle249
  Dir = (0,0,1)
  Solid = true
FEATURE [Part::Extrusion] Extrude121
  Base = -> Circle250
  Dir = (0,0,1)
  Solid = true
FEATURE [Part::Extrusion] Extrude122
  Base = -> Circle251
  Dir = (0,0,1)
  Solid = true
FEATURE [Part::Extrusion] Extrude123
  Base = -> Circle252
  Dir = (0,0,1)
  Solid = true
FEATURE [Part::Extrusion] Extrude124
  Base = -> Circle253
  Dir = (0,0,1)
  Solid = true
FEATURE [Part::Extrusion] Extrude125
  Base = -> Circle254
  Dir = (0,0,1)
  Solid = true
FEATURE [Part::Extrusion] Extrude126
  Base = -> Circle255
  Dir = (0,0,1)
  Solid = true
FEATURE [Part::Extrusion] Extrude127
  Base = -> Circle256
  Dir = (0,0,1)
  Solid = true
FEATURE [Part::Extrusion] Extrude128
  Base = -> Circle257
  Dir = (0,0,1)
  Solid = true
FEATURE [Part::Extrusion] Extrude129
  Base = -> Circle258
  Dir = (0,0,1)
  Solid = true
FEATURE [Part::Extrusion] Extrude130
  Base = -> Circle259
  Dir = (0,0,1)
  Solid = true
FEATURE [Part::Extrusion] Extrude131
  Base = -> Circle260
  Dir = (0,0,1)
  Solid = true
FEATURE [Part::Extrusion] Extrude132
  Base = -> Circle261
  Dir = (0,0,1)
  Solid = true
FEATURE [Part::Extrusion] Extrude133
  Base = -> Circle262
  Dir = (0,0,1)
  Solid = true
FEATURE [Part::Extrusion] Extrude134
  Base = -> Circle263
  Dir = (0,0,1)
  Solid = true
FEATURE [Part::Extrusion] Extrude135
  Base = -> Circle264
  Dir = (0,0,1)
  Solid = true
FEATURE [Part::Extrusion] Extrude136
  Base = -> Circle265
  Dir = (0,0,1)
  Solid = true
FEATURE [Part::Extrusion] Extrude137
  Base = -> Circle266
  Dir = (0,0,1)
  Solid = true
FEATURE [Part::Extrusion] Extrude138
  Base = -> Circle267
  Dir = (0,0,1)
  Solid = true
FEATURE [Part::Extrusion] Extrude139
  Base = -> Circle268
  Dir = (0,0,1)
  Solid = true
FEATURE [Part::Extrusion] Extrude140
  Base = -> Circle269
  Dir = (0,0,1)
  Solid = true
FEATURE [Part::Extrusion] Extrude141
  Base = -> Circle270
  Dir = (0,0,1)
  Solid = true
FEATURE [Part::Extrusion] Extrude142
  Base = -> Circle271
  Dir = (0,0,1)
  Solid = true
FEATURE [Part::Extrusion] Extrude143
  Base = -> Circle272
  Dir = (0,0,1)
  Solid = true
FEATURE [Part::Extrusion] Extrude144
  Base = -> Circle273
  Dir = (0,0,1)
  Solid = true
FEATURE [Part::Extrusion] Extrude145
  Base = -> Circle274
  Dir = (0,0,1)
  Solid = true
FEATURE [Part::Extrusion] Extrude146
  Base = -> Circle275
  Dir = (0,0,1)
  Solid = true
FEATURE [Part::Extrusion] Extrude147
  Base = -> Circle276
  Dir = (0,0,1)
  Solid = true
FEATURE [Part::Extrusion] Extrude148
  Base = -> Circle277
  Dir = (0,0,1)
  Solid = true
FEATURE [Part::Extrusion] Extrude149
  Base = -> Circle278
  Dir = (0,0,1)
  Solid = true
FEATURE [Part::Extrusion] Extrude150
  Base = -> Circle279
  Dir = (0,0,1)
  Solid = true
FEATURE [Part::Extrusion] Extrude151
  Base = -> Circle280
  Dir = (0,0,1)
  Solid = true
FEATURE [Part::Extrusion] Extrude152
  Base = -> Circle281
  Dir = (0,0,1)
  Solid = true
FEATURE [Part::Extrusion] Extrude153
  Base = -> Circle282
  Dir = (0,0,1)
  Solid = true
FEATURE [Part::Extrusion] Extrude154
  Base = -> Circle283
  Dir = (0,0,1)
  Solid = true
FEATURE [Part::Extrusion] Extrude155
  Base = -> Circle284
  Dir = (0,0,1)
  Solid = true
FEATURE [Part::Extrusion] Extrude156
  Base = -> Circle285
  Dir = (0,0,1)
  Solid = true
FEATURE [Part::Extrusion] Extrude157
  Base = -> Circle286
  Dir = (0,0,1)
  Solid = true
FEATURE [Part::Extrusion] Extrude158
  Base = -> Circle287
  Dir = (0,0,1)
  Solid = true
FEATURE [Part::Extrusion] Extrude159
  Base = -> Circle288
  Dir = (0,0,1)
  Solid = true
FEATURE [Part::Extrusion] Extrude160
  Base = -> Circle289
  Dir = (0,0,1)
  Solid = true
FEATURE [Part::Extrusion] Extrude161
  Base = -> Circle290
  Dir = (0,0,1)
  Solid = true
FEATURE [Part::Extrusion] Extrude162
  Base = -> Circle291
  Dir = (0,0,1)
  Solid = true
FEATURE [Part::Extrusion] Extrude163
  Base = -> Circle292
  Dir = (0,0,1)
  Solid = true
FEATURE [Part::Extrusion] Extrude164
  Base = -> Circle293
  Dir = (0,0,1)
  Solid = true
FEATURE [Part::Extrusion] Extrude165
  Base = -> Circle294
  Dir = (0,0,1)
  Solid = true
FEATURE [Part::Extrusion] Extrude166
  Base = -> Circle295
  Dir = (0,0,1)
  Solid = true
FEATURE [Part::Extrusion] Extrude167
  Base = -> Circle296
  Dir = (0,0,1)
  Solid = true
FEATURE [Part::Extrusion] Extrude168
  Base = -> Circle297
  Dir = (0,0,1)
  Solid = true
FEATURE [Part::Extrusion] Extrude169
  Base = -> Circle298
  Dir = (0,0,1)
  Solid = true
FEATURE [Part::Extrusion] Extrude170
  Base = -> Circle299
  Dir = (0,0,1)
  Solid = true
FEATURE [Part::Extrusion] Extrude171
  Base = -> Circle300
  Dir = (0,0,1)
  Solid = true
FEATURE [Part::Extrusion] Extrude172
  Base = -> Circle301
  Dir = (0,0,1)
  Solid = true
FEATURE [Part::Extrusion] Extrude173
  Base = -> Circle302
  Dir = (0,0,1)
  Solid = true
FEATURE [Part::Extrusion] Extrude174
  Base = -> Circle303
  Dir = (0,0,1)
  Solid = true
FEATURE [Part::Extrusion] Extrude175
  Base = -> Circle304
  Dir = (0,0,1)
  Solid = true
FEATURE [Part::Extrusion] Extrude176
  Base = -> Circle305
  Dir = (0,0,1)
  Solid = true
FEATURE [Part::Extrusion] Extrude177
  Base = -> Circle306
  Dir = (0,0,1)
  Solid = true
FEATURE [Part::Extrusion] Extrude178
  Base = -> Circle307
  Dir = (0,0,1)
  Solid = true
FEATURE [Part::Extrusion] Extrude179
  Base = -> Circle308
  Dir = (0,0,1)
  Solid = true
FEATURE [Part::Extrusion] Extrude180
  Base = -> Circle309
  Dir = (0,0,1)
  Solid = true
FEATURE [Part::Extrusion] Extrude181
  Base = -> Circle310
  Dir = (0,0,1)
  Solid = true
FEATURE [Part::Extrusion] Extrude182
  Base = -> Circle311
  Dir = (0,0,1)
  Solid = true
FEATURE [Part::Extrusion] Extrude183
  Base = -> Circle312
  Dir = (0,0,1)
  Solid = true
FEATURE [Part::Extrusion] Extrude184
  Base = -> Circle313
  Dir = (0,0,1)
  Solid = true
FEATURE [Part::Extrusion] Extrude185
  Base = -> Circle314
  Dir = (0,0,1)
  Solid = true
FEATURE [Part::Feature] Face
  shape: bbox 99.47 x 56.44 x 2e-07 mm, 1 faces, 0 solids (baked)
FEATURE [Part::Extrusion] Extrude186
  Base = -> Face
  Dir = (0,0,1)
  Solid = true
FEATURE [Part::FeaturePython] Clone002  label="Clone of Extrude126"  # Draft clone (typed FeaturePython)
  Objects = -> [Extrude126]
  Placement = pos=(0,-7.61999,0) rot=(0,0,1;0rad)
  Scale = (1,1,1)
FEATURE [Part::MultiFuse] Fusion
  Shapes = -> [Extrude,Extrude018,Extrude051,Extrude052,Extrude054,Extrude053,Extrude055,Extrude062,Extrude059,Extrude075,Extrude064,Extrude012,Extrude013,Extrude014,Extrude083,Extrude085,Extrude092,Extrude057,Extrude058,Extrude017,Extrude080,Extrude001,Extrude029,Extrude028,Extrude009,Extrude010,Extrude006,Extrude008,Extrude020,Extrude019,Extrude022,Extrude071,Extrude070,Extrude061,Extrude060,Extrude027,+151 more]
FEATURE [Part::Cut] Cut  label="PCB"
  Base = -> Extrude186
  Tool = -> Fusion
FEATURE [Part::Feature] Part__Feature010  label="Fusion001"
  Placement = pos=(85.8049,-81.037,8) rot=(0,0,1;0rad)
  shape: bbox 10 x 13 x 11 mm, 119 faces (baked)
FEATURE [Part::FeaturePython] Clone003  label="Clone of Fusion001"  # Draft clone (typed FeaturePython)
  Objects = -> [Part__Feature010]
  Placement = pos=(95.9649,-81.037,8) rot=(0,0,1;0rad)
  Scale = (1,1,1)
FEATURE [Part::FeaturePython] Clone004  label="Clone of Fusion002"  # Draft clone (typed FeaturePython)
  Objects = -> [Part__Feature010]
  Placement = pos=(106.125,-81.037,8) rot=(0,0,1;0rad)
  Scale = (1,1,1)
FEATURE [Part::FeaturePython] Clone005  label="Clone of Fusion003"  # Draft clone (typed FeaturePython)
  Objects = -> [Part__Feature010]
  Placement = pos=(116.285,-81.037,8) rot=(0,0,1;0rad)
  Scale = (1,1,1)
FEATURE [Part::FeaturePython] Clone006  label="Clone of Fusion004"  # Draft clone (typed FeaturePython)
  Objects = -> [Part__Feature010]
  Placement = pos=(126.445,-81.037,8) rot=(0,0,1;0rad)
  Scale = (1,1,1)
FEATURE [Part::Feature] Compound001
  Placement = pos=(143.95,-73.2281,1) rot=(0,0,1;0rad)
  shape: bbox 8.213 x 1.9 x 4.7 mm, 19 faces, 3 solids (baked)
FEATURE [Part::FeaturePython] Clone007  label="Clone of Compound001"  # Draft clone (typed FeaturePython)
  Objects = -> [Compound001]
  Placement = pos=(100.897,-92.0749,1) rot=(0,0,1;0rad)
  Scale = (1,1,1)
FEATURE [Part::FeaturePython] Clone008  label="Clone of Compound003"  # Draft clone (typed FeaturePython)
  Objects = -> [Compound001]
  Placement = pos=(90.7369,-92.0749,1) rot=(0,0,1;0rad)
  Scale = (1,1,1)
FEATURE [Part::FeaturePython] Clone009  label="Clone of Compound004"  # Draft clone (typed FeaturePython)
  Objects = -> [Compound001]
  Placement = pos=(90.7369,-92.0749,1) rot=(0,0,1;0rad)
  Scale = (1,1,1)
FEATURE [Part::FeaturePython] Clone010  label="Clone of Compound005"  # Draft clone (typed FeaturePython)
  Objects = -> [Compound001]
  Placement = pos=(121.217,-92.0749,1) rot=(0,0,1;0rad)
  Scale = (1,1,1)
FEATURE [Part::FeaturePython] Clone011  label="Clone of Compound006"  # Draft clone (typed FeaturePython)
  Objects = -> [Compound001]
  Placement = pos=(111.057,-92.0749,1) rot=(0,0,1;0rad)
  Scale = (1,1,1)
FEATURE [Part::FeaturePython] Clone012  label="Clone of Compound007"  # Draft clone (typed FeaturePython)
  Objects = -> [Compound001]
  Placement = pos=(143.95,-64.0841,1) rot=(0,0,1;0rad)
  Scale = (1,1,1)
FEATURE [Part::FeaturePython] Clone013  label="Clone of Compound008"  # Draft clone (typed FeaturePython)
  Objects = -> [Compound001]
  Placement = pos=(131.377,-92.0749,1) rot=(0,0,1;0rad)
  Scale = (1,1,1)
FEATURE [Part::FeaturePython] Clone014  label="Clone of Compound009"  # Draft clone (typed FeaturePython)
  Objects = -> [Compound001]
  Placement = pos=(143.95,-70.1801,1) rot=(0,0,1;0rad)
  Scale = (1,1,1)
FEATURE [Part::FeaturePython] Clone015  label="Clone of Compound010"  # Draft clone (typed FeaturePython)
  Objects = -> [Compound001]
  Placement = pos=(143.95,-67.1321,1) rot=(0,0,1;0rad)
  Scale = (1,1,1)
FEATURE [Part::FeaturePython] Clone016  label="Clone of Compound011"  # Draft clone (typed FeaturePython)
  Objects = -> [Compound001]
  Placement = pos=(143.95,-76.2761,1) rot=(0,0,1;0rad)
  Scale = (1,1,1)
FEATURE [Part::FeaturePython] Clone017  label="Clone of Compound012"  # Draft clone (typed FeaturePython)
  Objects = -> [Compound001]
  Placement = pos=(131.377,-66.0399,1) rot=(0,0,1;0rad)
  Scale = (1,1,1)
FEATURE [Part::FeaturePython] Clone018  label="Clone of Compound013"  # Draft clone (typed FeaturePython)
  Objects = -> [Compound001]
  Placement = pos=(143.95,-85.4201,1) rot=(0,0,1;0rad)
  Scale = (1,1,1)
FEATURE [Part::FeaturePython] Clone019  label="Clone of Compound014"  # Draft clone (typed FeaturePython)
  Objects = -> [Compound001]
  Placement = pos=(121.217,-66.0399,1) rot=(0,0,1;0rad)
  Scale = (1,1,1)
FEATURE [Part::FeaturePython] Clone020  label="Clone of Compound015"  # Draft clone (typed FeaturePython)
  Objects = -> [Compound001]
  Placement = pos=(143.95,-82.3721,1) rot=(0,0,1;0rad)
  Scale = (1,1,1)
FEATURE [Part::FeaturePython] Clone021  label="Clone of Compound016"  # Draft clone (typed FeaturePython)
  Objects = -> [Compound001]
  Placement = pos=(111.057,-66.0399,1) rot=(0,0,1;0rad)
  Scale = (1,1,1)
FEATURE [Part::FeaturePython] Clone022  label="Clone of Compound017"  # Draft clone (typed FeaturePython)
  Objects = -> [Compound001]
  Placement = pos=(100.897,-66.0399,1) rot=(0,0,1;0rad)
  Scale = (1,1,1)
FEATURE [Part::FeaturePython] Clone023  label="Clone of Compound018"  # Draft clone (typed FeaturePython)
  Objects = -> [Compound001]
  Placement = pos=(90.7369,-66.0399,1) rot=(0,0,1;0rad)
  Scale = (1,1,1)
FEATURE [Part::FeaturePython] Clone024  label="Clone of Compound019"  # Draft clone (typed FeaturePython)
  Objects = -> [Compound001]
  Placement = pos=(143.95,-79.3241,1) rot=(0,0,1;0rad)
  Scale = (1,1,1)
FEATURE [Part::Feature] Part__Feature011  label="Head"
  shape: bbox 4.9 x 3.424 x 4.83 mm, 8 faces (baked)
FEATURE [Part::Feature] Part__Feature012  label="Pins"
  Placement = pos=(0,0,0) rot=(1,0,0;1.5708rad)
  shape: bbox 0.5 x 0.5 x 5.54 mm, 6 faces (baked)
FEATURE [Part::Feature] Part__Feature013  label="Pins001"
  Placement = pos=(0,0,0) rot=(1,0,0;1.5708rad)
  shape: bbox 0.5 x 0.5 x 5.54 mm, 6 faces (baked)
FEATURE [Part::Feature] Part__Feature014  label="Pins002"
  Placement = pos=(0,0,0) rot=(1,0,0;1.5708rad)
  shape: bbox 0.5 x 0.5 x 5.54 mm, 6 faces (baked)
FEATURE [Part::Compound] Compound
  Links = -> [Part__Feature014,Part__Feature012,Part__Feature013,Part__Feature011]
  Placement = pos=(131.455,-87.6299,-1) rot=(0,0,1;3.14159rad)
FEATURE [Part::FeaturePython] Clone025  label="Clone of Compound"  # Draft clone (typed FeaturePython)
  Objects = -> [Compound]
  Placement = pos=(100.975,-87.6299,-1) rot=(0,0,1;3.14159rad)
  Scale = (1,1,1)
FEATURE [Part::FeaturePython] Clone026  label="Clone of Compound020"  # Draft clone (typed FeaturePython)
  Objects = -> [Compound]
  Placement = pos=(121.295,-87.6299,-1) rot=(0,0,1;3.14159rad)
  Scale = (1,1,1)
FEATURE [Part::FeaturePython] Clone027  label="Clone of Compound021"  # Draft clone (typed FeaturePython)
  Objects = -> [Compound]
  Placement = pos=(111.135,-87.6299,-1) rot=(0,0,1;3.14159rad)
  Scale = (1,1,1)
FEATURE [Part::FeaturePython] Clone028  label="Clone of Compound022"  # Draft clone (typed FeaturePython)
  Objects = -> [Compound]
  Placement = pos=(90.8149,-87.6299,-1) rot=(0,0,1;3.14159rad)
  Scale = (1,1,1)
FEATURE [App::DocumentObjectGroup] Group  label="Parts"
  Group = -> [Clone001,Clone,Compound003,Part__Feature009,Compound002,Part__Feature010,Clone003,Clone004,Clone005,Clone006,Compound001,Clone007,Clone008,Clone009,Clone010,Clone011,Clone012,Clone013,Clone014,Clone015,Clone016,Clone017,Clone018,Clone019,Clone020,Clone021,Clone022,Clone023,Clone024,Compound,Clone025,Clone026,Clone027,Clone028]
FEATURE [App::FeaturePython] Dimension  # Draft dimension (typed FeaturePython)
  Dimline = (136.058,-52.9919,9)
  Direction = (0,0,0)
  Distance = 50.04
  End = (136.094,-56.5749,9)
  Normal = (0,0,1)
  Start = (86.0541,-56.5749,9)
FEATURE [App::FeaturePython] Dimension001  # Draft dimension (typed FeaturePython)
  Dimline = (166.073,-45.7342,1)
  Direction = (0,0,0)
  Distance = 85.3441
  End = (170.28,-51.308,1)
  Normal = (0,0,1)
  Start = (84.9359,-51.308,1)
FEATURE [App::FeaturePython] Dimension002  # Draft dimension (typed FeaturePython)
  Dimline = (171.949,-42.1513,1)
  Direction = (0,0,0)
  Distance = 90.4239
  End = (172.72,-48.768,1)
  Normal = (0,0,1)
  Start = (82.2959,-48.768,1)
FEATURE [App::FeaturePython] Dimension003  # Draft dimension (typed FeaturePython)
  Dimline = (74.3836,-99.7045,1)
  Direction = (0,0,0)
  Distance = 51.308
  End = (82.2959,-100.076,1)
  Normal = (0,0,1)
  Start = (82.2959,-48.768,1)
FEATURE [App::FeaturePython] Dimension004  # Draft dimension (typed FeaturePython)
  Dimline = (78.1137,-97.1524,1)
  Direction = (0,0,0)
  Distance = 46.2279
  End = (84.9359,-97.5359,1)
  Normal = (0,0,1)
  Start = (84.9359,-51.308,1)
FEATURE [App::FeaturePython] Dimension005  # Draft dimension (typed FeaturePython)
  Dimline = (83.17,-60.0276,9)
  Direction = (0,0,0)
  Distance = 5.07996
  End = (86.0541,-61.6549,9)
  Normal = (0,0,1)
  Start = (86.0541,-56.5749,9)
FEATURE [App::FeaturePython] Dimension006  # Draft dimension (typed FeaturePython)
  Dimline = (83.1699,-61.6549,9)
  Direction = (0,0,0)
  Distance = 7.49066
  End = (86.0541,-69.1456,9)
  Normal = (0,0,1)
  Start = (86.0541,-61.6549,9)
FEATURE [App::FeaturePython] Dimension007  # Draft dimension (typed FeaturePython)
  Dimline = (83.1699,-69.1456,9)
  Direction = (0,0,0)
  Distance = 10.5609
  End = (86.0541,-79.7065,9)
  Normal = (0,0,1)
  Start = (86.0541,-69.1456,9)
FEATURE [Part::Part2DObjectPython] Line  # Draft 2D object (typed FeaturePython)
  ChamferSize = 0
  Closed = false
  End = (83.1699,-69.1456,9)
  FilletRadius = 0
  Length = 6.4048
  MakeFace = true
  Points = (2) [(89.5747,-69.1456,9),(83.1699,-69.1456,9)]
  Start = (89.5747,-69.1456,9)
  Subdivisions = 0
FEATURE [Part::Part2DObjectPython] Line001  # Draft 2D object (typed FeaturePython)
  ChamferSize = 0
  Closed = false
  End = (83.1699,-79.7065,9)
  FilletRadius = 0
  Length = 4.5942
  MakeFace = true
  Points = (2) [(87.7641,-79.7065,9),(83.1699,-79.7065,9)]
  Start = (87.7641,-79.7065,9)
  Subdivisions = 0
FEATURE [Part::Compound] Compound004
  Links = -> [Clone001,Clone,Clone019,Clone023,Part__Feature010,Clone005,Clone025,Clone010,Clone006,Part__Feature009,Clone017,Clone013,Compound002,Cut,Clone018,Clone027,Clone016,Clone008,Clone009,Clone012,Compound001,Clone022,Clone004,Clone015,Clone026,Clone007,Clone021,Clone020,Clone028,Clone014,Compound003,Clone011,Clone003,Clone024,Compound]
FEATURE [Drawing::FeatureViewPart] View
  Direction = (0,0,1)
  HiddenWidth = 0.15
  LineWidth = 0.35
  Rotation = 0
  Scale = 2
  ShowHiddenLines = false
  ShowSmoothLines = true
  Source = -> Compound004
  Tolerance = 0.05
  ViewResult = <blob: 299634 chars omitted>
  Visible = true
  X = -100
  Y = -60
FEATURE [Drawing::FeatureViewPart] Ortho002  label="Ortho_-1_1"
  Direction = (0.57735,-0.57735,0.57735)
  HiddenWidth = 0.15
  LineWidth = 0.35
  Rotation = 60
  Scale = 0.75
  ShowHiddenLines = false
  ShowSmoothLines = true
  Source = -> Compound004
  Tolerance = 0.05
  ViewResult = <blob: 474621 chars omitted>
  Visible = true
  X = 48
  Y = 110
FEATURE [Drawing::FeatureViewPython] ViewDimension002  # drawing view (typed FeaturePython)
  Direction = (0,0,0)
  FillStyle = 0
  FontSize = 5
  LineStyle = 0
  LineWidth = 0.35
  Rotation = 0
  Scale = 2
  Source = -> Dimension002
  ViewResult = <g id="ViewDimension002" transform="rotate(0.0,-100.0,-60.0) translate(-100.0,-60.0) scale(2.0,-2.0)"><path d="M 82.2959445822 -48.7679535559 L 82.2959445822 -42.1512947083 L 172.719883691 -42.1512947083 L 172.719883691 -48.7679535559" fill="none" stroke="#000000" stroke-width="0.175 px" style="stroke-width:0.175;stroke-miterlimit:4;stroke-dasharray:none" freecad:basepoint1="82.2959445822 -48.7679535559" freecad:basepoint2="172.719883691 -48.7679535559" freecad:dimpoint="82.2959445822 -42.1512947083"/>\n<path transform="rotate(-0.0,82.2959445822,-42.1512947083) translate(82.2959445822,-42.1512947083) scale(0.466666666667,0.466666666667)" freecad:skip="1" fill="#000000" stroke="none" style="stroke-miterlimit:4;stroke-dasharray:none" d="M 0 0 L 4 1 L 4 -1 Z"/>\n<path transform="rotate(180.0,172.719883691,-42.1512947083) translate(172.719883691,-42.1512947083) scale(0.466666666667,0.466666666667)" freecad:skip="1" fill="#000000" stroke="none" style="stroke-miterlimit:4;stroke-dasharray:none" d="M 0 0 L 4 1 L 4 -1 Z"/>\n<text fill="#000000" font-size="1.25" style="text-anchor:middle;text-align:center;font-family:" transform="rotate(-0.0,127.507914137,-41.6512947083) translate(127.507914137,-41.6512947083) scale(1,-1) " freecad:skip="1">\n90 mm</text>\n</g>
  Visible = true
  X = -100
  Y = -60
FEATURE [Drawing::FeatureViewPython] ViewDimension001  # drawing view (typed FeaturePython)
  Direction = (0,0,0)
  FillStyle = 0
  FontSize = 5
  LineStyle = 0
  LineWidth = 0.35
  Rotation = 0
  Scale = 2
  Source = -> Dimension001
  ViewResult = <g id="ViewDimension001" transform="rotate(0.0,-100.0,-60.0) translate(-100.0,-60.0) scale(2.0,-2.0)"><path d="M 84.9359 -51.308 L 84.9359 -45.7342376709 L 170.28 -45.7342376709 L 170.28 -51.308" fill="none" stroke="#000000" stroke-width="0.175 px" style="stroke-width:0.175;stroke-miterlimit:4;stroke-dasharray:none" freecad:basepoint1="84.9359 -51.308" freecad:basepoint2="170.28 -51.308" freecad:dimpoint="84.9359 -45.7342376709"/>\n<path transform="rotate(-0.0,84.9359,-45.7342376709) translate(84.9359,-45.7342376709) scale(0.466666666667,0.466666666667)" freecad:skip="1" fill="#000000" stroke="none" style="stroke-miterlimit:4;stroke-dasharray:none" d="M 0 0 L 4 1 L 4 -1 Z"/>\n<path transform="rotate(180.0,170.28,-45.7342376709) translate(170.28,-45.7342376709) scale(0.466666666667,0.466666666667)" freecad:skip="1" fill="#000000" stroke="none" style="stroke-miterlimit:4;stroke-dasharray:none" d="M 0 0 L 4 1 L 4 -1 Z"/>\n<text fill="#000000" font-size="1.25" style="text-anchor:middle;text-align:center;font-family:" transform="rotate(-0.0,127.60795,-45.2342376709) translate(127.60795,-45.2342376709) scale(1,-1) " freecad:skip="1">\n85,3 mm</text>\n</g>
  Visible = true
  X = -100
  Y = -60
FEATURE [Drawing::FeatureViewPython] ViewDimension006  # drawing view (typed FeaturePython)
  Direction = (0,0,0)
  FillStyle = 0
  FontSize = 5
  LineStyle = 0
  LineWidth = 0.35
  Rotation = 0
  Scale = 2
  Source = -> Dimension006
  ViewResult = <g id="ViewDimension006" transform="rotate(0.0,-100.0,-60.0) translate(-100.0,-60.0) scale(2.0,-2.0)"><path d="M 86.0541411101 -61.6549401306 L 83.1699384065 -61.6549243016 L 83.1698972964 -69.145584171 L 86.0541 -69.1456" fill="none" stroke="#000000" stroke-width="0.175 px" style="stroke-width:0.175;stroke-miterlimit:4;stroke-dasharray:none" freecad:basepoint1="86.0541411101 -61.6549401306" freecad:basepoint2="86.0541 -69.1456" freecad:dimpoint="83.1699384065 -61.6549243016"/>\n<path transform="rotate(-90.0003139287,83.1699384065,-61.6549243016) translate(83.1699384065,-61.6549243016) scale(0.466666666667,0.466666666667)" freecad:skip="1" fill="#000000" stroke="none" style="stroke-miterlimit:4;stroke-dasharray:none" d="M 0 0 L 4 1 L 4 -1 Z"/>\n<path transform="rotate(89.9996860713,83.1698972964,-69.145584171) translate(83.1698972964,-69.145584171) scale(0.466666666667,0.466666666667)" freecad:skip="1" fill="#000000" stroke="none" style="stroke-miterlimit:4;stroke-dasharray:none" d="M 0 0 L 4 1 L 4 -1 Z"/>\n<text fill="#000000" font-size="1.25" style="text-anchor:middle;text-align:center;font-family:" transform="rotate(-90.0003139287,83.6699178515,-65.4002569804) translate(83.6699178515,-65.4002569804) scale(1,-1) " freecad:skip="1">\n7,5 mm</text>\n</g>
  Visible = true
  X = -100
  Y = -60
FEATURE [Drawing::FeatureViewPython] ViewDimension007  # drawing view (typed FeaturePython)
  Direction = (0,0,0)
  FillStyle = 0
  FontSize = 5
  LineStyle = 0
  LineWidth = 0.35
  Rotation = 0
  Scale = 2
  Source = -> Dimension007
  ViewResult = <g id="ViewDimension007" transform="rotate(0.0,-100.0,-60.0) translate(-100.0,-60.0) scale(2.0,-2.0)"><path d="M 86.0541 -69.1456 L 83.1698972964 -69.1456 L 83.1698972964 -79.7065 L 86.0541 -79.7065" fill="none" stroke="#000000" stroke-width="0.175 px" style="stroke-width:0.175;stroke-miterlimit:4;stroke-dasharray:none" freecad:basepoint1="86.0541 -69.1456" freecad:basepoint2="86.0541 -79.7065" freecad:dimpoint="83.1698972964 -69.1456"/>\n<path transform="rotate(-90.0,83.1698972964,-69.1456) translate(83.1698972964,-69.1456) scale(0.466666666667,0.466666666667)" freecad:skip="1" fill="#000000" stroke="none" style="stroke-miterlimit:4;stroke-dasharray:none" d="M 0 0 L 4 1 L 4 -1 Z"/>\n<path transform="rotate(90.0,83.1698972964,-79.7065) translate(83.1698972964,-79.7065) scale(0.466666666667,0.466666666667)" freecad:skip="1" fill="#000000" stroke="none" style="stroke-miterlimit:4;stroke-dasharray:none" d="M 0 0 L 4 1 L 4 -1 Z"/>\n<text fill="#000000" font-size="1.25" style="text-anchor:middle;text-align:center;font-family:" transform="rotate(-90.0,83.6698972964,-74.42605) translate(83.6698972964,-74.42605) scale(1,-1) " freecad:skip="1">\n10 mm</text>\n</g>
  Visible = true
  X = -100
  Y = -60
FEATURE [Drawing::FeatureViewPython] ViewDimension005  # drawing view (typed FeaturePython)
  Direction = (0,0,0)
  FillStyle = 0
  FontSize = 5
  LineStyle = 0
  LineWidth = 0.35
  Rotation = 0
  Scale = 2
  Source = -> Dimension005
  ViewResult = <g id="ViewDimension005" transform="rotate(0.0,-100.0,-60.0) translate(-100.0,-60.0) scale(2.0,-2.0)"><path d="M 86.0541411101 -56.5749401306 L 83.1699795169 -56.5749167902 L 83.1699384068 -61.6548766596 L 86.0541 -61.6549" fill="none" stroke="#000000" stroke-width="0.175 px" style="stroke-width:0.175;stroke-miterlimit:4;stroke-dasharray:none" freecad:basepoint1="86.0541411101 -56.5749401306" freecad:basepoint2="86.0541 -61.6549" freecad:dimpoint="83.1699795169 -56.5749167902"/>\n<path transform="rotate(89.9995363514,83.1699795169,-56.5749167902) translate(83.1699795169,-56.5749167902) scale(0.466666666667,0.466666666667)" freecad:skip="1" fill="#000000" stroke="none" style="stroke-miterlimit:4;stroke-dasharray:none" d="M 0 0 L 4 1 L 4 -1 Z"/>\n<path transform="rotate(269.999536351,83.1699384068,-61.6548766596) translate(83.1699384068,-61.6548766596) scale(0.466666666667,0.466666666667)" freecad:skip="1" fill="#000000" stroke="none" style="stroke-miterlimit:4;stroke-dasharray:none" d="M 0 0 L 4 1 L 4 -1 Z"/>\n<text fill="#000000" font-size="1.25" style="text-anchor:middle;text-align:center;font-family:" transform="rotate(-90.0004636486,83.6699589618,-59.1149007712) translate(83.6699589618,-59.1149007712) scale(1,-1) " freecad:skip="1">\n5 mm</text>\n</g>
  Visible = true
  X = -100
  Y = -60
FEATURE [Drawing::FeatureViewPython] ViewDimension004  # drawing view (typed FeaturePython)
  Direction = (0,0,0)
  FillStyle = 0
  FontSize = 5
  LineStyle = 0
  LineWidth = 0.35
  Rotation = 0
  Scale = 2
  Source = -> Dimension004
  ViewResult = <g id="ViewDimension004" transform="rotate(0.0,-100.0,-60.0) translate(-100.0,-60.0) scale(2.0,-2.0)"><path d="M 84.9359 -51.308 L 78.1136779785 -51.308 L 78.1136779785 -97.5359 L 84.9359 -97.5359" fill="none" stroke="#000000" stroke-width="0.175 px" style="stroke-width:0.175;stroke-miterlimit:4;stroke-dasharray:none" freecad:basepoint1="84.9359 -51.308" freecad:basepoint2="84.9359 -97.5359" freecad:dimpoint="78.1136779785 -51.308"/>\n<path transform="rotate(-90.0,78.1136779785,-51.308) translate(78.1136779785,-51.308) scale(0.466666666667,0.466666666667)" freecad:skip="1" fill="#000000" stroke="none" style="stroke-miterlimit:4;stroke-dasharray:none" d="M 0 0 L 4 1 L 4 -1 Z"/>\n<path transform="rotate(90.0,78.1136779785,-97.5359) translate(78.1136779785,-97.5359) scale(0.466666666667,0.466666666667)" freecad:skip="1" fill="#000000" stroke="none" style="stroke-miterlimit:4;stroke-dasharray:none" d="M 0 0 L 4 1 L 4 -1 Z"/>\n<text fill="#000000" font-size="1.25" style="text-anchor:middle;text-align:center;font-family:" transform="rotate(-90.0,78.6136779785,-74.42195) translate(78.6136779785,-74.42195) scale(1,-1) " freecad:skip="1">\n46,2 mm</text>\n</g>
  Visible = true
  X = -100
  Y = -60
FEATURE [Drawing::FeatureViewPython] ViewLine  # drawing view (typed FeaturePython)
  Direction = (0,0,0)
  FillStyle = 0
  FontSize = 5
  LineStyle = 0
  LineWidth = 0.35
  Rotation = 0
  Scale = 2
  Source = -> Line
  ViewResult = <g id="ViewLine" transform="rotate(0.0,-100.0,-60.0) translate(-100.0,-60.0) scale(2.0,-2.0)"><path id="Line_w0000"  d="M 89.5747 -69.1456 L 83.1698972964 -69.145584171 " stroke="#000000" stroke-width="0.175 px" style="stroke-width:0.175;stroke-miterlimit:4;stroke-dasharray:none;fill:none;fill-rule: evenodd "/>\n</g>
  Visible = true
  X = -100
  Y = -60
FEATURE [Drawing::FeatureViewPython] ViewLine001  # drawing view (typed FeaturePython)
  Direction = (0,0,0)
  FillStyle = 0
  FontSize = 5
  LineStyle = 0
  LineWidth = 0.35
  Rotation = 0
  Scale = 2
  Source = -> Line001
  ViewResult = <g id="ViewLine001" transform="rotate(0.0,-100.0,-60.0) translate(-100.0,-60.0) scale(2.0,-2.0)"><path id="Line001_w0000"  d="M 87.7641 -79.7065 L 83.1698972964 -79.7065 " stroke="#000000" stroke-width="0.175 px" style="stroke-width:0.175;stroke-miterlimit:4;stroke-dasharray:none;fill:none;fill-rule: evenodd "/>\n</g>
  Visible = true
  X = -100
  Y = -60
FEATURE [Drawing::FeatureViewPython] ViewDimension003  # drawing view (typed FeaturePython)
  Direction = (0,0,0)
  FillStyle = 0
  FontSize = 5
  LineStyle = 0
  LineWidth = 0.35
  Rotation = 0
  Scale = 2
  Source = -> Dimension003
  ViewResult = <g id="ViewDimension003" transform="rotate(0.0,-100.0,-60.0) translate(-100.0,-60.0) scale(2.0,-2.0)"><path d="M 82.2959445822 -48.7679535559 L 74.383644104 -48.7679535559 L 74.383644104 -100.075904693 L 82.2959445822 -100.075904693" fill="none" stroke="#000000" stroke-width="0.175 px" style="stroke-width:0.175;stroke-miterlimit:4;stroke-dasharray:none" freecad:basepoint1="82.2959445822 -48.7679535559" freecad:basepoint2="82.2959445822 -100.075904693" freecad:dimpoint="74.383644104 -48.7679535559"/>\n<path transform="rotate(-90.0,74.383644104,-48.7679535559) translate(74.383644104,-48.7679535559) scale(0.466666666667,0.466666666667)" freecad:skip="1" fill="#000000" stroke="none" style="stroke-miterlimit:4;stroke-dasharray:none" d="M 0 0 L 4 1 L 4 -1 Z"/>\n<path transform="rotate(90.0,74.383644104,-100.075904693) translate(74.383644104,-100.075904693) scale(0.466666666667,0.466666666667)" freecad:skip="1" fill="#000000" stroke="none" style="stroke-miterlimit:4;stroke-dasharray:none" d="M 0 0 L 4 1 L 4 -1 Z"/>\n<text fill="#000000" font-size="1.25" style="text-anchor:middle;text-align:center;font-family:" transform="rotate(-90.0,74.883644104,-74.4219291245) translate(74.883644104,-74.4219291245) scale(1,-1) " freecad:skip="1">\n51 mm</text>\n</g>
  Visible = true
  X = -100
  Y = -60
FEATURE [Drawing::FeatureViewPython] ViewDimension  # drawing view (typed FeaturePython)
  Direction = (0,0,0)
  FillStyle = 0
  FontSize = 5
  LineStyle = 0
  LineWidth = 0.35
  Rotation = 0
  Scale = 2
  Source = -> Dimension
  ViewResult = <g id="ViewDimension" transform="rotate(0.0,-100.0,-60.0) translate(-100.0,-60.0) scale(2.0,-2.0)"><path d="M 86.0541411101 -56.5749401306 L 86.0541411101 -52.9919052124 L 136.09414111 -52.9919052124 L 136.09414111 -56.5749401306" fill="none" stroke="#000000" stroke-width="0.175 px" style="stroke-width:0.175;stroke-miterlimit:4;stroke-dasharray:none" freecad:basepoint1="86.0541411101 -56.5749401306" freecad:basepoint2="136.09414111 -56.5749401306" freecad:dimpoint="86.0541411101 -52.9919052124"/>\n<path transform="rotate(-0.0,86.0541411101,-52.9919052124) translate(86.0541411101,-52.9919052124) scale(0.466666666667,0.466666666667)" freecad:skip="1" fill="#000000" stroke="none" style="stroke-miterlimit:4;stroke-dasharray:none" d="M 0 0 L 4 1 L 4 -1 Z"/>\n<path transform="rotate(180.0,136.09414111,-52.9919052124) translate(136.09414111,-52.9919052124) scale(0.466666666667,0.466666666667)" freecad:skip="1" fill="#000000" stroke="none" style="stroke-miterlimit:4;stroke-dasharray:none" d="M 0 0 L 4 1 L 4 -1 Z"/>\n<text fill="#000000" font-size="1.25" style="text-anchor:middle;text-align:center;font-family:" transform="rotate(-0.0,111.07414111,-52.4919052124) translate(111.07414111,-52.4919052124) scale(1,-1) " freecad:skip="1">\n50 mm</text>\n</g>
  Visible = true
  X = -100
  Y = -60
FEATURE [Drawing::FeaturePage] Page
  EditableTexts = Angel LM  | 20/02/2016 | 2:1 | 75g | Bobachest | 1.0 | BC1 | 1
  Group = -> [View,ViewLine,ViewDimension007,ViewDimension006,ViewDimension005,ViewDimension004,ViewDimension001,ViewDimension,ViewDimension002,ViewDimension003,ViewLine001,Ortho002]
